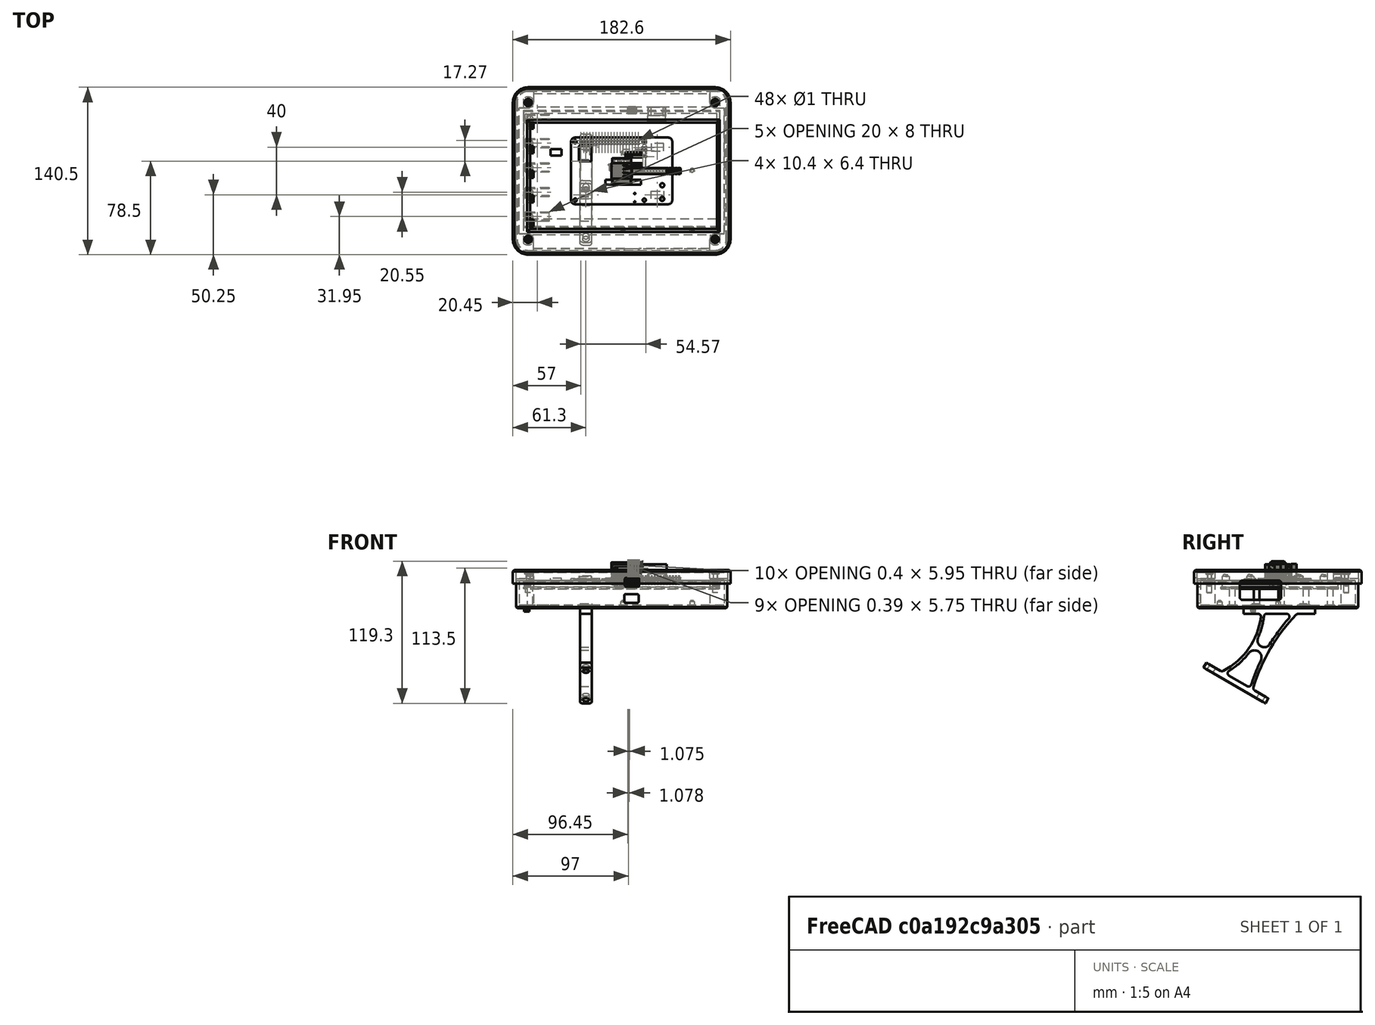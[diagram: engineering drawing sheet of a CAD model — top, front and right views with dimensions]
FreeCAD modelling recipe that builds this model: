
FCSTD DOCUMENT  (FreeCAD 0.19R24212 (Git))
Label: rpi_screen
License: Creative Commons Attribution
LicenseURL: http://creativecommons.org/licenses/by/4.0/
objects: Part::Feature×166, Part::Compound2×67, App::Part×24, App::Link×22, Sketcher::SketchObject×20, PartDesign::SubShapeBinder×13, PartDesign::Pocket×12, App::FeaturePython×10, PartDesign::Pad×9, Part::FeaturePython×8, PartDesign::Plane×5, PartDesign::Mirrored×4, PartDesign::Body×4, TechDraw::DrawViewDimension×4, PartDesign::Chamfer×3, PartDesign::LinearPattern×3, PartDesign::Fillet×3, Mesh::Feature×3, App::DocumentObjectGroup×2, PartDesign::MultiTransform×2, +9 more types
note: 286 computed .brp shape members not serialized (recipe doc carries the construction recipe); baked Part::Feature solids carry a one-line shape summary decoded from their .brp

FEATURE [Part::Feature] Compound  label="3"
  shape: bbox 164.9 x 124.4 x 20.55 mm, 570 faces, 2 solids (baked)
FEATURE [Part::Feature] Solid  label="pcb"
  shape: bbox 85 x 56 x 1.6 mm, 74 faces (baked)
FEATURE [Part::Feature] Solid001  label="shield"
  shape: bbox 5.846 x 7.775 x 3.404 mm, 350 faces (baked)
FEATURE [Part::Feature] Solid002  label="socket_housing"
  shape: bbox 4.232 x 6.852 x 2.152 mm, 218 faces (baked)
FEATURE [Part::Feature] Solid003  label="socket_plate"
  shape: bbox 3.38 x 6.8 x 0.31 mm, 84 faces (baked)
FEATURE [Part::Feature] Solid004  label="terminal"
  shape: bbox 3.22 x 0.35 x 1.72 mm, 36 faces (baked)
FEATURE [Part::Compound2] Compound001  label="shield:1"
  Links = -> [Solid001]
FEATURE [Part::Compound2] Compound002  label="socket_housing:1"
  Links = -> [Solid002]
FEATURE [Part::Compound2] Compound003  label="socket_plate:1"
  Links = -> [Solid003]
FEATURE [App::Link] Link  label="terminal:1"
  ElementCount = 5
  LinkedObject = -> Solid004
  PlacementList = 5 placements: [(0,0,0),(-4.44089e-15,-1.3,0),(-4.44089e-15,-0.65,0),(-4.44089e-15,0.65,0),(-4.44089e-15,1.3,0)]
  ScaleList = (5) [(1,1,1),(1,1,1),(1,1,1),(1,1,1),(1,1,1)]
  ShowElement = false
FEATURE [App::Part] Part  label="micro_usb_connector v17"
  Group = -> [Compound001,Compound002,Compound003,Link,Solid001,Solid002,Solid003]
  Origin = -> Origin
FEATURE [Part::Feature] Solid005  label="shell"
  shape: bbox 12 x 1.42 x 11.4 mm, 293 faces (baked)
FEATURE [Part::Compound2] Compound004  label="housing"
  Links = -> [Solid005]
FEATURE [Part::Feature] Solid006  label="base"
  shape: bbox 11.86 x 1.428 x 10.41 mm, 183 faces (baked)
FEATURE [Part::Feature] Solid007  label="Component12"
  shape: bbox 0.75 x 1.138 x 7.857 mm, 54 faces (baked)
FEATURE [Part::Feature] Solid008  label="Component13"
  shape: bbox 0.75 x 1.164 x 8.156 mm, 54 faces (baked)
FEATURE [Part::Feature] Solid009  label="Component14"
  shape: bbox 0.75 x 1.133 x 7.808 mm, 54 faces (baked)
FEATURE [Part::Feature] Solid010  label="Component15"
  shape: bbox 1.567 x 1.275 x 4.5 mm, 37 faces (baked)
FEATURE [Part::Feature] Solid011  label="Component16"
  shape: bbox 1.37 x 1.25 x 4.893 mm, 26 faces (baked)
FEATURE [App::Link] Link001  label="Component12:1"
  ElementCount = 5
  LinkedObject = -> Solid007
  PlacementList = 5 placements: [(0,0,0),(-2.2,0,-4.44089e-15),(-4.4,0,-4.44089e-15),(-6.6,0,-4.44089e-15),(-7.7,0,-4.44089e-15)]
  ScaleList = (5) [(1,1,1),(1,1,1),(1,1,1),(1,1,1),(1,1,1)]
  ShowElement = false
FEATURE [Part::Compound2] Compound005  label="Component13:1"
  Links = -> [Solid008]
  Placement = pos=(-1.1,6.29e-14,5.33e-14) rot=(0,0,1;0rad)
FEATURE [App::Link] Link002  label="Component14:1"
  ElementCount = 2
  LinkedObject = -> Solid009
  PlacementList = 2 placements: [(-3.3,3.34455e-14,5.32907e-14),(-5.5,2.90046e-14,5.32907e-14)]
  ScaleList = (2) [(1,1,1),(1,1,1)]
  ShowElement = false
FEATURE [Part::Compound2] Compound006  label="Component15:1"
  Links = -> [Solid010]
FEATURE [Part::Compound2] Compound007  label="Component16:1"
  Links = -> [Solid011]
FEATURE [App::Part] Part001  label="leads"
  Group = -> [Link001,Compound005,Link002,Compound006,Compound007,Solid008,Solid010,Solid011]
  Origin = -> Origin001
FEATURE [Part::Compound2] Compound008  label="housing:1"
  Links = -> [Compound004]
FEATURE [Part::Compound2] Compound009  label="base:1"
  Links = -> [Solid006]
FEATURE [Part::Compound2] Compound010  label="leads:1"
  Links = -> [Part001]
FEATURE [App::Part] Part002  label="sd_card_slot_molex v11"
  Group = -> [Compound008,Compound009,Compound010,Compound004,Solid005,Solid006,Part001]
  Origin = -> Origin002
FEATURE [Part::Feature] Compound011  label="pins"
  shape: bbox 48.9 x 3.175 x 10 mm, 560 faces, 40 solids (baked)
FEATURE [Part::Feature] Solid012  label="Component67"
  shape: bbox 50.81 x 5.089 x 2.549 mm, 625 faces (baked)
FEATURE [Part::Compound2] Compound012  label="spacers"
  Links = -> [Solid012]
FEATURE [Part::Compound2] Compound013  label="pins:1"
  Links = -> [Compound011]
FEATURE [Part::Compound2] Compound014  label="spacers:1"
  Links = -> [Compound012]
FEATURE [App::Part] Part003  label="Pin Header 20x2 TH Pitch 2.54mm v1"
  Group = -> [Compound013,Compound014,Compound011,Compound012,Solid012]
  Origin = -> Origin003
FEATURE [Part::Feature] Solid013  label="outer"
  shape: bbox 17 x 15.83 x 20.03 mm, 628 faces (baked)
FEATURE [Part::Feature] Solid014  label="back_shell"
  shape: bbox 2.8 x 13.7 x 13.5 mm, 64 faces (baked)
FEATURE [Part::Feature] Solid015  label="mid_cover"
  shape: bbox 8.5 x 12.4 x 5.09 mm, 174 faces (baked)
FEATURE [Part::Compound2] Compound015  label="outer:1"
  Links = -> [Solid013]
FEATURE [Part::Compound2] Compound016  label="back_shell:1"
  Links = -> [Solid014]
FEATURE [Part::Compound2] Compound017  label="mid_cover:1"
  Links = -> [Solid015]
FEATURE [App::Part] Part004  label="shell"
  Group = -> [Compound015,Compound016,Compound017,Solid013,Solid014,Solid015]
  Origin = -> Origin004
FEATURE [Part::Feature] Solid016  label="Component5"
  shape: bbox 16.28 x 12.43 x 15.05 mm, 451 faces (baked)
FEATURE [Part::Compound2] Compound018  label="Component4"
  Links = -> [Solid016]
FEATURE [Part::Feature] Solid017  label="top_lead"
  shape: bbox 14.29 x 1.538 x 16.6 mm, 94 faces (baked)
FEATURE [Part::Feature] Solid018  label="bottom_lead"
  shape: bbox 11.67 x 1.538 x 7.97 mm, 92 faces (baked)
FEATURE [App::Link] Link003  label="top_lead:1"
  ElementCount = 4
  LinkedObject = -> Solid017
  PlacementList = 4 placements: [(0,0,0),(0,-2.5,0),(0,-7,0),(0,-4.5,0)]
  ScaleList = (4) [(1,1,1),(1,1,1),(1,1,1),(1,1,1)]
  ShowElement = false
FEATURE [App::Link] Link004  label="bottom_lead:1"
  ElementCount = 4
  LinkedObject = -> Solid018
  PlacementList = 4 placements: [(0,0,0),(0,-7,0),(0,-2.5,0),(0,-4.5,0)]
  ScaleList = (4) [(1,1,1),(1,1,1),(1,1,1),(1,1,1)]
  ShowElement = false
FEATURE [App::Part] Part005  label="leads"
  Group = -> [Link003,Link004]
  Origin = -> Origin005
FEATURE [Part::Compound2] Compound019  label="shell:1"
  Links = -> [Part004]
FEATURE [Part::Compound2] Compound020  label="Component4:1"
  Links = -> [Compound018]
FEATURE [Part::Compound2] Compound021  label="leads:1"
  Links = -> [Part005]
FEATURE [App::Part] Part006  label="USB-A-stack-1x2 v23"
  Group = -> [Compound019,Compound020,Compound021,Part004,Compound018,Solid016,Part005]
  Origin = -> Origin006
FEATURE [App::Link] Link005  label="outer:1"
  LinkedObject = -> Solid013
FEATURE [App::Link] Link006  label="back_shell:1"
  LinkedObject = -> Solid014
FEATURE [App::Link] Link007  label="mid_cover:1"
  LinkedObject = -> Solid015
FEATURE [App::Part] Part007  label="shell"
  Group = -> [Link005,Link006,Link007]
  Origin = -> Origin007
FEATURE [App::Link] Link008  label="Component4"
  LinkedObject = -> Solid016
FEATURE [App::Link] Link009  label="top_lead:1"
  ElementCount = 4
  LinkedObject = -> Solid017
  PlacementList = 4 placements: [(0,0,0),(0,-2.5,0),(0,-7,0),(0,-4.5,0)]
  ScaleList = (4) [(1,1,1),(1,1,1),(1,1,1),(1,1,1)]
  ShowElement = false
FEATURE [App::Link] Link010  label="bottom_lead:1"
  ElementCount = 4
  LinkedObject = -> Solid018
  PlacementList = 4 placements: [(0,0,0),(0,-7,0),(0,-2.5,0),(0,-4.5,0)]
  ScaleList = (4) [(1,1,1),(1,1,1),(1,1,1),(1,1,1)]
  ShowElement = false
FEATURE [App::Part] Part008  label="leads"
  Group = -> [Link009,Link010]
  Origin = -> Origin008
FEATURE [Part::Compound2] Compound022  label="shell:1"
  Links = -> [Part007]
FEATURE [Part::Compound2] Compound023  label="Component4:1"
  Links = -> [Link008]
FEATURE [Part::Compound2] Compound024  label="leads:1"
  Links = -> [Part008]
FEATURE [App::Part] Part009  label="USB-A-stack-1x2 v23"
  Group = -> [Compound022,Compound023,Compound024,Part007,Link008,Part008]
  Origin = -> Origin009
FEATURE [Part::Feature] Compound025  label="te_1-1734248-5"
  shape: bbox 22.4 x 5.68 x 5.072 mm, 978 faces, 17 solids (baked)
FEATURE [Part::Feature] Compound026  label="pins"
  shape: bbox 3.175 x 3.175 x 10 mm, 56 faces, 4 solids (baked)
FEATURE [Part::Feature] Solid019  label="Component5"
  shape: bbox 5.089 x 5.089 x 2.549 mm, 67 faces (baked)
FEATURE [Part::Compound2] Compound027  label="spacers"
  Links = -> [Solid019]
FEATURE [Part::Compound2] Compound028  label="pins:1"
  Links = -> [Compound026]
FEATURE [Part::Compound2] Compound029  label="spacers:1"
  Links = -> [Compound027]
FEATURE [App::Part] Part010  label="Pin Header 2x2 TH Pitch 2.54mm v1"
  Group = -> [Compound028,Compound029,Compound026,Compound027,Solid019]
  Origin = -> Origin010
FEATURE [Part::Feature] Compound030  label="SOP-3_1.6mm"
  shape: bbox 1.6 x 1.559 x 0.6498 mm, 68 faces, 4 solids (baked)
FEATURE [Part::Feature] Solid020  label="shell"
  shape: bbox 16.2 x 21.35 x 16.35 mm, 324 faces (baked)
FEATURE [Part::Feature] Compound031  label="rj45"
  shape: bbox 13.46 x 13.45 x 4.487 mm, 170 faces, 9 solids (baked)
FEATURE [Part::Feature] Compound032  label="magnetics"
  shape: bbox 11.5 x 6.5 x 11.5 mm, 40 faces, 2 solids (baked)
FEATURE [Part::Feature] Compound033  label="leads"
  shape: bbox 13.9 x 7.95 x 8.72 mm, 162 faces, 9 solids (baked)
FEATURE [Part::Compound2] Compound034  label="rj45:1"
  Links = -> [Compound031]
FEATURE [Part::Compound2] Compound035  label="magnetics:1"
  Links = -> [Compound032]
FEATURE [Part::Compound2] Compound036  label="leads:1"
  Links = -> [Compound033]
FEATURE [App::Part] Part011  label="wiring"
  Group = -> [Compound034,Compound035,Compound036,Compound031,Compound032,Compound033]
  Origin = -> Origin011
FEATURE [Part::Feature] Solid021  label="base"
  shape: bbox 15.6 x 20.75 x 16.5 mm, 165 faces (baked)
FEATURE [Part::Feature] Compound037  label="led_org"
  shape: bbox 3.048 x 5.198 x 4.864 mm, 48 faces, 2 solids (baked)
FEATURE [Part::Feature] Compound038
  shape: bbox 13.8 x 4.169 x 2.2 mm, 12 faces, 2 solids (baked)
FEATURE [App::Link] Link011  label="led_org:1"
  ElementCount = 2
  LinkedObject = -> Compound037
  PlacementList = 2 placements: [(-5.37,0,2.2),(5.37,-8.88178e-15,2.2)]
  ScaleList = (2) [(1,1,1),(1,1,1)]
  ShowElement = false
FEATURE [App::Part] Part012  label="lights"
  Group = -> [Link011,Compound038]
  Origin = -> Origin012
FEATURE [Part::Compound2] Compound039  label="shell:1"
  Links = -> [Solid020]
FEATURE [Part::Compound2] Compound040  label="wiring:1"
  Links = -> [Part011]
FEATURE [Part::Compound2] Compound041  label="base:1"
  Links = -> [Solid021]
FEATURE [Part::Compound2] Compound042  label="lights:1"
  Links = -> [Part012]
FEATURE [App::Part] Part013  label="EDAC_1743_RJ45_TH v18"
  Group = -> [Compound039,Compound040,Compound041,Compound042,Solid020,Part011,Solid021,Part012]
  Origin = -> Origin013
FEATURE [Part::Feature] Compound043  label="qfn32_5mm v3"
  shape: bbox 5.2 x 5.2 x 0.55 mm, 218 faces, 33 solids (baked)
FEATURE [Part::Feature] Compound044  label="qfn48_9mm v3"
  shape: bbox 9 x 9 x 0.6 mm, 314 faces, 49 solids (baked)
FEATURE [Part::Feature] Compound045  label="TSOP-6 2mm v1"
  shape: bbox 2 x 2.009 x 0.7998 mm, 110 faces, 7 solids (baked)
FEATURE [Part::Feature] Compound046  label="TSOP-6 3mm v3"
  shape: bbox 3 x 2.913 x 0.7997 mm, 110 faces, 7 solids (baked)
FEATURE [Part::Feature] Solid022  label="Component1"
  shape: bbox 2.5 x 1.75 x 0.4 mm, 6 faces (baked)
FEATURE [Part::Feature] Compound047  label="lead"
  shape: bbox 2.7 x 1.95 x 0.12 mm, 96 faces, 16 solids (baked)
FEATURE [Part::Compound2] Compound048  label="Component1:1"
  Links = -> [Solid022]
  Placement = pos=(0,-1.3e-15,0) rot=(0,0,1;0rad)
FEATURE [Part::Compound2] Compound049  label="lead:1"
  Links = -> [Compound047]
  Placement = pos=(0,-1.3e-15,0) rot=(0,0,1;0rad)
FEATURE [App::Part] Part014  label="qfp16_3x2mm v5"
  Group = -> [Compound048,Compound049,Solid022,Compound047]
  Origin = -> Origin014
FEATURE [Part::Feature] Solid023  label="Component73"
  shape: bbox 10.5 x 13 x 2 mm, 46 faces (baked)
FEATURE [Part::Compound2] Compound050  label="wifi"
  Links = -> [Solid023]
FEATURE [Part::Feature] Compound051  label="qfn80_12mm v3"
  shape: bbox 12 x 12 x 0.6 mm, 506 faces, 81 solids (baked)
FEATURE [Part::Feature] Compound052  label="Component2"
  shape: bbox 3.2 x 2.5 x 0.3 mm, 44 faces, 4 solids (baked)
FEATURE [Part::Feature] Solid024  label="Component3"
  shape: bbox 3.2 x 2.5 x 0.4 mm, 30 faces (baked)
FEATURE [Part::Feature] Solid025  label="Component4"
  shape: bbox 2.9 x 2.3 x 0.2 mm, 35 faces (baked)
FEATURE [Part::Feature] Solid026  label="Component5"
  shape: bbox 2.5 x 1.9 x 0.2 mm, 35 faces (baked)
FEATURE [Part::Compound2] Compound053  label="Component2:1"
  Links = -> [Compound052]
FEATURE [Part::Compound2] Compound054  label="Component3:1"
  Links = -> [Solid024]
FEATURE [Part::Compound2] Compound055  label="Component4:1"
  Links = -> [Solid025]
FEATURE [Part::Compound2] Compound056  label="Component5:1"
  Links = -> [Solid026]
FEATURE [App::Part] Part015  label="crystal_dfn4 v1"
  Group = -> [Compound053,Compound054,Compound055,Compound056,Compound052,Solid024,Solid025,Solid026]
  Origin = -> Origin015
FEATURE [Part::Feature] Compound057  label="bcm2837 v8"
  shape: bbox 14 x 14 x 1.6 mm, 565 faces, 83 solids (baked)
FEATURE [Part::Feature] Compound058  label="wlbga140_5mm v2"
  shape: bbox 4.47 x 5.27 x 0.51 mm, 446 faces, 141 solids (baked)
FEATURE [Part::Feature] Compound059  label="cap0603_03 v2"
  shape: bbox 2.303 x 0.9021 x 0.802 mm, 98 faces, 3 solids (baked)
FEATURE [Part::Feature] Compound060  label="cap0402 v1"
  shape: bbox 1.367 x 0.6001 x 0.5 mm, 98 faces, 3 solids (baked)
FEATURE [Part::Feature] Compound061  label="resistor_0402 v1"
  shape: bbox 1.268 x 0.6007 x 0.3506 mm, 56 faces, 3 solids (baked)
FEATURE [Part::Feature] Compound062  label="cap1206 v4"
  shape: bbox 4.144 x 2.009 x 1.609 mm, 98 faces, 3 solids (baked)
FEATURE [Part::Feature] Compound063  label="ind2520 v1"
  shape: bbox 2.606 x 2.106 x 1.53 mm, 54 faces, 3 solids (baked)
FEATURE [Part::Feature] Compound064  label="ledra_0603 v2"
  shape: bbox 1.2 x 1.7 x 0.6 mm, 51 faces, 5 solids (baked)
FEATURE [Part::Feature] Solid027  label="tip_lead"
  shape: bbox 9.124 x 7.155 x 8.351 mm, 90 faces (baked)
FEATURE [Part::Feature] Solid028  label="Component2"
  shape: bbox 13.26 x 2.5 x 4.339 mm, 52 faces (baked)
FEATURE [Part::Feature] Solid029  label="Component3"
  shape: bbox 11.45 x 1.401 x 8.705 mm, 48 faces (baked)
FEATURE [Part::Feature] Solid030  label="Component4"
  shape: bbox 8.225 x 1.505 x 8.701 mm, 48 faces (baked)
FEATURE [Part::Feature] Solid031
  shape: bbox 15.01 x 7.008 x 7.255 mm, 115 faces (baked)
FEATURE [Part::Compound2] Compound065  label="tip_lead:1"
  Links = -> [Solid027]
FEATURE [Part::Compound2] Compound066  label="Component2:1"
  Links = -> [Solid028]
FEATURE [Part::Compound2] Compound067  label="Component3:1"
  Links = -> [Solid029]
FEATURE [Part::Compound2] Compound068  label="Component4:1"
  Links = -> [Solid030]
FEATURE [App::Part] Part016  label="pj-322 v8"
  Group = -> [Compound065,Compound066,Compound067,Compound068,Solid031,Solid027,Solid028,Solid029,Solid030]
  Origin = -> Origin016
FEATURE [Part::Feature] Compound069  label="SOP-3 v1"
  shape: bbox 3 x 2.713 x 1.05 mm, 68 faces, 4 solids (baked)
FEATURE [Part::Feature] Compound070  label="SOP-3 2.5mm v3"
  shape: bbox 2.6 x 2.213 x 0.6497 mm, 68 faces, 4 solids (baked)
FEATURE [Part::Feature] Compound071  label="capar2_1013 v1"
  shape: bbox 1.474 x 1.006 x 0.6909 mm, 170 faces, 5 solids (baked)
FEATURE [Part::Feature] Solid032  label="Component2"
  shape: bbox 15 x 11.55 x 8.274 mm, 347 faces (baked)
FEATURE [Part::Feature] Compound072
  shape: bbox 14.9 x 10.35 x 6.23 mm, 710 faces, 3 solids (baked)
FEATURE [Part::Compound2] Compound073  label="Component2:1"
  Links = -> [Solid032]
FEATURE [App::Part] Part017  label="molex hdmi smt v8"
  Group = -> [Compound073,Compound072,Solid032]
  Origin = -> Origin017
FEATURE [Part::Feature] Compound074  label="TSOP-2 4mm v2"
  shape: bbox 3.5 x 5.913 x 2.05 mm, 42 faces, 3 solids (baked)
FEATURE [Part::Compound2] Compound075  label="pcb:1"
  Links = -> [Solid]
FEATURE [Part::Compound2] Compound076  label="micro_usb_connector v17:1"
  Links = -> [Part]
  Placement = pos=(-31.9022,-25.6898,1.6) rot=(0,0,-1;1.5708rad)
FEATURE [Part::Compound2] Compound077  label="sd_card_slot_molex v11:1"
  Links = -> [Part002]
  Placement = pos=(-35.5259,0.0195459,0) rot=(0.57735,0.57735,-0.57735;4.18879rad)
FEATURE [Part::Compound2] Compound078  label="Pin Header 20x2 TH Pitch 2.54mm v1:1"
  Links = -> [Part003]
  Placement = pos=(-34.0983,24.2639,1.6) rot=(0,0,1;0rad)
FEATURE [Part::Compound2] Compound079  label="USB-A-stack-1x2 v23:1"
  Links = -> [Part006]
  Placement = pos=(35.9589,0.615691,1.6) rot=(0,0,1;0rad)
FEATURE [Part::Compound2] Compound080  label="USB-A-stack-1x2 v23:2"
  Links = -> [Part009]
  Placement = pos=(35.9589,19.0157,1.6) rot=(0,0,1;0rad)
FEATURE [App::Link] Link012  label="te_1-1734248-5:1"
  ElementCount = 2
  LinkedObject = -> Compound025
  PlacementList = 2 placements: [(-38.8804,0.0129527,1.58),(2.68293,-16.6511,1.58)]
  ScaleList = (2) [(1,1,1),(1,1,1)]
  ShowElement = false
FEATURE [Part::Compound2] Compound081  label="Pin Header 2x2 TH Pitch 2.54mm v1:1"
  Links = -> [Part010]
  Placement = pos=(17.7441,18.3632,1.6) rot=(0,0,1;0rad)
FEATURE [App::Link] Link013  label="SOP-3_1.6mm:1"
  ElementCount = 4
  LinkedObject = -> Compound030
  PlacementList = 4 placements: [(-40.8905,-10.8155,-8.403e-14),(-40.814,-18.4594,-8.42382e-14),(-16.6511,-13.2136,1.6),(-16.6511,-11.1136,1.6)]
  ScaleList = (4) [(1,1,1),(1,1,1),(1,1,1),(1,1,1)]
  ShowElement = false
FEATURE [Part::Compound2] Compound082  label="EDAC_1743_RJ45_TH v18:1"
  Links = -> [Part013]
  Placement = pos=(34.0212,-17.8853,1.5) rot=(0,0,1;1.5708rad)
FEATURE [Part::Compound2] Compound083  label="qfn32_5mm v3:1"
  Links = -> [Compound043]
  Placement = pos=(-29.2738,-12.9325,1.6) rot=(0,0,1;0rad)
FEATURE [Part::Compound2] Compound084  label="qfn48_9mm v3:1"
  Links = -> [Compound044]
  Placement = pos=(19.0565,-0.238451,1.6) rot=(0,0,1;0rad)
FEATURE [Part::Compound2] Compound085  label="TSOP-6 2mm v1:1"
  Links = -> [Compound045]
  Placement = pos=(14.2657,-10.6917,1.6) rot=(0,0,1;0rad)
FEATURE [Part::Compound2] Compound086  label="TSOP-6 3mm v3:1"
  Links = -> [Compound046]
  Placement = pos=(12.2743,17.7497,1.6) rot=(0,0,-1;1.5708rad)
FEATURE [Part::Compound2] Compound087  label="qfp16_3x2mm v5:1"
  Links = -> [Part014]
  Placement = pos=(-32.0595,4.91492,1.6) rot=(0,0,1;0rad)
FEATURE [Part::Compound2] Compound088  label="wifi:1"
  Links = -> [Compound050]
FEATURE [Part::Compound2] Compound089  label="qfn80_12mm v3:1"
  Links = -> [Compound051]
  Placement = pos=(0.978423,5.52192,4e-16) rot=(0,1,0;3.14159rad)
FEATURE [App::Link] Link014  label="crystal_dfn4 v1:1"
  ElementCount = 2
  LinkedObject = -> Part015
  PlacementList = 2 placements: [(-16.2394,-5.98323,-1.98875e-15),(11.4677,1.47513,6.08602e-15)]
  ScaleList = (2) [(1,1,1),(1,1,1)]
  ShowElement = false
FEATURE [Part::Compound2] Compound090  label="bcm2837 v8:1"
  Links = -> [Compound057]
  Placement = pos=(-15.6667,3.46142,1.6) rot=(0,0,1;0rad)
FEATURE [Part::Compound2] Compound091  label="wlbga140_5mm v2:1"
  Links = -> [Compound058]
  Placement = pos=(-30.4818,13.9472,1.6) rot=(0,0,1;0rad)
FEATURE [App::Link] Link015  label="cap0603_03 v2:1"
  ElementCount = 15
  LinkedObject = -> Compound059
  PlacementList = 15 placements: [(6.20173,12.0599,1.6),(-22.2778,-12.3124,1.6),(-22.2778,-13.6124,1.6),(-36.2901,-12.0302,1.6),(-36.2901,-13.3302,1.6),(-22.6025,-16.7071,1.6),(-31.9549,-9.07389,1.6),(-36.0614,-9.11907,1.6),(-16.8344,0.818806,-0.000650846),(-16.6946,6.87647,-0.000650846),(-40.1331,-7.59203,-0.000650846),(13.801,-4.8435,-0.000650846),(22.8947,7.02239,-0.000650846),(21.8412,4.90662,-0.000650846),+1 more]
  ScaleList = (15) [(1,1,1),(1,1,1),(1,1,1),(1,1,1),(1,1,1),(1,1,1),(1,1,1),(1,1,1),(1,1,1),(1,1,1),(1,1,1),(1,1,1),(1,1,1),(1,1,1),(1,1,1)]
  ShowElement = false
FEATURE [App::Link] Link016  label="cap0402 v1:1"
  ElementCount = 90
  LinkedObject = -> Compound060
  PlacementList = 90 placements: [(-1.68462,0.200917,1.6),(-3.61651,0.117459,1.6),(5.92099,0.258461,1.6),(3.98909,0.175003,1.6),(-2.07285,4.84427,1.6),(-3.73362,5.74918,1.6),(-1.7854,5.75983,1.6),(1.09272,2.11766,1.6),(-0.660114,2.54963,1.6),(-0.904466,7.62354,1.6),(4.53291,2.97061,1.6),(6.38708,2.45158,1.6),(6.35031,5.20918,1.6),(4.97764,5.87101,1.6),(2.18297,-0.0835865,1.6),(2.55763,11.2194,1.6),(0.128581,11.1773,1.6),+73 more]
  ScaleList = (90) [(1,1,1),(1,1,1),(1,1,1),(1,1,1),(1,1,1),(1,1,1),(1,1,1),(1,1,1),(1,1,1),(1,1,1),(1,1,1),(1,1,1),(1,1,1),(1,1,1),(1,1,1),(1,1,1),(1,1,1),(1,1,1),+72 more]
  ShowElement = false
FEATURE [App::Link] Link017  label="resistor_0402 v1:1"
  ElementCount = 57
  LinkedObject = -> Compound061
  PlacementList = 57 placements: [(13.5093,-0.0741632,1.6),(13.5249,2.06113,1.6),(13.7425,5.61112,1.6),(20.9328,7.1813,1.6),(21.7458,7.19308,1.6),(12.3038,-10.6968,1.6),(12.2911,-11.6977,1.6),(16.2822,-10.7348,1.6),(16.2949,-11.7484,1.6),(12.2922,-13.2114,1.6),(12.2703,-14.0987,1.6),(6.27571,-16.9459,1.6),(17.4427,-5.70402,1.6),(18.7432,-5.71563,1.6),(20.5313,-5.75046,1.6),(21.9594,-5.73885,1.6),(24.5889,-0.571464,1.6),+40 more]
  ScaleList = (57) [(1,1,1),(1,1,1),(1,1,1),(1,1,1),(1,1,1),(1,1,1),(1,1,1),(1,1,1),(1,1,1),(1,1,1),(1,1,1),(1,1,1),(1,1,1),(1,1,1),(1,1,1),(1,1,1),(1,1,1),(1,1,1),+39 more]
  ShowElement = false
FEATURE [App::Link] Link018  label="cap1206 v4:1"
  ElementCount = 11
  LinkedObject = -> Compound062
  PlacementList = 11 placements: [(7.98424,7.88741,1.6),(-25.9964,-19.3212,1.6),(-36.5363,-17.3583,1.6),(-22.3159,-8.61657,1.6),(-20.0447,-8.61657,1.6),(-26.8904,-24.2006,1.6),(23.3268,10.3578,1.6),(23.886,19.0543,1.6),(25.6036,-6.14103,1.6),(16.4512,-16.6927,1.6),(17.7022,-20.3318,1.6)]
  ScaleList = (11) [(1,1,1),(1,1,1),(1,1,1),(1,1,1),(1,1,1),(1,1,1),(1,1,1),(1,1,1),(1,1,1),(1,1,1),(1,1,1)]
  ShowElement = false
FEATURE [App::Link] Link019  label="ind2520 v1:1"
  ElementCount = 4
  LinkedObject = -> Compound063
  PlacementList = 4 placements: [(-33.8028,-16.3221,1.6),(-33.9058,-9.58662,1.6),(-24.8087,-16.2044,1.6),(-24.7831,-9.50136,1.6)]
  ScaleList = (4) [(1,1,1),(1,1,1),(1,1,1),(1,1,1)]
  ShowElement = false
FEATURE [App::Link] Link020  label="ledra_0603 v2:1"
  ElementCount = 2
  LinkedObject = -> Compound064
  PlacementList = 2 placements: [(-41.4207,-16.546,1.6),(-41.4207,-20.2157,1.6)]
  ScaleList = (2) [(1,1,1),(1,1,1)]
  ShowElement = false
FEATURE [Part::Compound2] Compound092  label="pj-322 v8:1"
  Links = -> [Part016]
  Placement = pos=(11.1035,-22.958,1.6) rot=(0,0,1;1.5708rad)
FEATURE [Part::Compound2] Compound093  label="SOP-3 v1:1"
  Links = -> [Compound069]
  Placement = pos=(-17.0907,-15.6679,1.6) rot=(0,0,1;1.5708rad)
FEATURE [Part::Compound2] Compound094  label="SOP-3 2.5mm v3:1"
  Links = -> [Compound070]
  Placement = pos=(7.13922,-13.3247,1.6) rot=(0,0,1;0rad)
FEATURE [App::Link] Link021  label="capar2_1013 v1:1"
  ElementCount = 4
  LinkedObject = -> Compound071
  PlacementList = 4 placements: [(-11.0324,-15.0395,1.6),(-9.5324,-15.0395,1.6),(-8.0324,-15.0395,1.6),(-6.5324,-15.0395,1.6)]
  ScaleList = (4) [(1,1,1),(1,1,1),(1,1,1),(1,1,1)]
  ShowElement = false
FEATURE [Part::Compound2] Compound095  label="molex hdmi smt v8:1"
  Links = -> [Part017]
  Placement = pos=(-10.5578,-23.8041,1.6) rot=(0,0,1;0rad)
FEATURE [Part::Compound2] Compound096  label="TSOP-2 4mm v2:1"
  Links = -> [Compound074]
  Placement = pos=(-23.9074,-24.0113,1.6) rot=(0,0,1;0rad)
FEATURE [App::Part] Part018  label="raspberry_pi_3_b_plus v38"
  Group = -> [Compound075,Compound076,Compound077,Compound078,Compound079,Compound080,Link012,Compound081,Link013,Compound082,Compound083,Compound084,Compound085,Compound086,Compound087,Compound088,Compound089,Link014,Compound090,Compound091,Link015,Link016,Link017,Link018,Link019,Link020,Compound092,Compound093,Compound094,Link021,Compound095,Compound096,Solid,Part,Part002,Part003,Part006,Part009,Part010,+16 more]
  Origin = -> Origin018
  Placement = pos=(40.15,24.4,17.75) rot=(1,0,0;3.14159rad)
FEATURE [Part::Feature] Solid033  label="1"
  shape: bbox 2.5 x 5 x 0.9 mm, 6 faces (baked)
FEATURE [Part::Feature] Solid034  label="2"
  shape: bbox 2.5 x 5 x 0.9 mm, 6 faces (baked)
FEATURE [Part::Feature] Solid035  label="3"
  shape: bbox 2.5 x 5 x 0.9 mm, 6 faces (baked)
FEATURE [Part::Feature] Solid036  label="4"
  shape: bbox 2.5 x 5 x 0.9 mm, 6 faces (baked)
FEATURE [Part::Feature] Solid037  label="6"
  shape: bbox 0.4 x 0.2 x 6.5 mm, 6 faces (baked)
FEATURE [Part::Feature] Solid038  label="7"
  shape: bbox 0.4 x 0.2 x 6.5 mm, 6 faces (baked)
FEATURE [Part::Feature] Solid039  label="8"
  shape: bbox 0.4 x 0.2 x 6.5 mm, 6 faces (baked)
FEATURE [Part::Feature] Solid040  label="9"
  shape: bbox 0.4 x 0.2 x 6.5 mm, 6 faces (baked)
FEATURE [Part::Feature] Solid041  label="10"
  shape: bbox 0.4 x 0.2 x 6.5 mm, 6 faces (baked)
FEATURE [Part::Feature] Solid042  label="11"
  shape: bbox 0.4 x 0.2 x 6.5 mm, 6 faces (baked)
FEATURE [Part::Feature] Solid043  label="12"
  shape: bbox 0.4 x 0.2 x 6.5 mm, 6 faces (baked)
FEATURE [Part::Feature] Solid044  label="13"
  shape: bbox 0.4 x 0.2 x 6.5 mm, 6 faces (baked)
FEATURE [Part::Feature] Solid045  label="14"
  shape: bbox 0.4 x 0.2 x 6.5 mm, 6 faces (baked)
FEATURE [Part::Feature] Solid046  label="15"
  shape: bbox 0.4 x 0.2 x 6.5 mm, 6 faces (baked)
FEATURE [Part::Feature] Solid047  label="16"
  shape: bbox 0.4 x 0.2 x 6.5 mm, 6 faces (baked)
FEATURE [Part::Feature] Solid048  label="17"
  shape: bbox 0.4 x 0.2 x 6.5 mm, 6 faces (baked)
FEATURE [Part::Feature] Solid049  label="18"
  shape: bbox 0.4 x 0.2 x 6.5 mm, 6 faces (baked)
FEATURE [Part::Feature] Solid050  label="19"
  shape: bbox 0.4 x 0.2 x 6.5 mm, 6 faces (baked)
FEATURE [Part::Feature] Solid051  label="20"
  shape: bbox 0.4 x 0.2 x 6.5 mm, 6 faces (baked)
FEATURE [Part::Feature] Solid052  label="21"
  shape: bbox 0.4 x 0.2 x 6.5 mm, 6 faces (baked)
FEATURE [Part::Feature] Solid053  label="22"
  shape: bbox 0.4 x 0.2 x 6.5 mm, 6 faces (baked)
FEATURE [Part::Feature] Solid054  label="23"
  shape: bbox 0.4 x 0.2 x 6.5 mm, 6 faces (baked)
FEATURE [Part::Feature] Solid055  label="24"
  shape: bbox 0.4 x 0.2 x 6.5 mm, 6 faces (baked)
FEATURE [Part::Feature] Solid056  label="25"
  shape: bbox 0.4 x 0.2 x 6.5 mm, 6 faces (baked)
FEATURE [Part::Feature] Solid057  label="26"
  shape: bbox 0.4 x 0.2 x 6.5 mm, 6 faces (baked)
FEATURE [Part::Feature] Solid058  label="27"
  shape: bbox 0.4 x 0.4828 x 5.951 mm, 23 faces (baked)
FEATURE [Part::Feature] Solid059  label="28"
  shape: bbox 0.4 x 0.4828 x 5.951 mm, 23 faces (baked)
FEATURE [Part::Feature] Solid060  label="29"
  shape: bbox 0.4 x 0.5578 x 6.051 mm, 25 faces (baked)
FEATURE [Part::Feature] Solid061  label="32"
  shape: bbox 0.4 x 0.5578 x 6.051 mm, 25 faces (baked)
FEATURE [Part::Feature] Solid062  label="33"
  shape: bbox 0.4 x 0.5578 x 6.051 mm, 25 faces (baked)
FEATURE [Part::Feature] Solid063  label="34"
  shape: bbox 0.4 x 0.5578 x 6.051 mm, 25 faces (baked)
FEATURE [Part::Feature] Solid064  label="35"
  shape: bbox 0.4 x 0.5578 x 6.051 mm, 25 faces (baked)
FEATURE [Part::Feature] Solid065  label="36"
  shape: bbox 0.4 x 0.5578 x 6.051 mm, 25 faces (baked)
FEATURE [Part::Feature] Solid066  label="37"
  shape: bbox 0.4 x 0.5578 x 6.051 mm, 25 faces (baked)
FEATURE [Part::Feature] Solid067  label="38"
  shape: bbox 0.4 x 0.5578 x 6.051 mm, 25 faces (baked)
FEATURE [Part::Feature] Solid068  label="39"
  shape: bbox 0.4 x 0.5578 x 6.051 mm, 25 faces (baked)
FEATURE [Part::Feature] Solid069  label="95"
  shape: bbox 1 x 1 x 1 mm, 6 faces (baked)
FEATURE [Part::Feature] Solid070  label="96"
  shape: bbox 1 x 1 x 1 mm, 6 faces (baked)
FEATURE [Part::Feature] Solid071  label="97"
  shape: bbox 1 x 1 x 1 mm, 6 faces (baked)
FEATURE [Part::Feature] Solid072  label="98"
  shape: bbox 1 x 1 x 1 mm, 6 faces (baked)
FEATURE [Part::Feature] Solid073  label="103"
  shape: bbox 20 x 18 x 0.9 mm, 26 faces (baked)
FEATURE [Part::Feature] Solid074  label="32"
  shape: bbox 0.4 x 0.5578 x 6.051 mm, 25 faces (baked)
FEATURE [Part::Feature] Solid075  label="27"
  shape: bbox 0.4 x 0.4828 x 5.951 mm, 23 faces (baked)
FEATURE [Part::Feature] Solid076  label="1"
  shape: bbox 13.3 x 3.9 x 6.525 mm, 432 faces (baked)
FEATURE [Part::Feature] Solid077  label="27"
  shape: bbox 0.4 x 0.4828 x 5.951 mm, 23 faces (baked)
FEATURE [Part::Feature] Solid078  label="27"
  shape: bbox 0.4 x 0.4828 x 5.951 mm, 23 faces (baked)
FEATURE [Part::Feature] Solid079  label="27"
  shape: bbox 0.4 x 0.4828 x 5.951 mm, 23 faces (baked)
FEATURE [Part::Feature] Solid080  label="27"
  shape: bbox 0.4 x 0.4828 x 5.951 mm, 23 faces (baked)
FEATURE [Part::Feature] Solid081  label="27"
  shape: bbox 0.4 x 0.4828 x 5.951 mm, 23 faces (baked)
FEATURE [Part::Feature] Solid082  label="27"
  shape: bbox 0.4 x 0.4828 x 5.951 mm, 23 faces (baked)
FEATURE [Part::Feature] Solid083  label="27"
  shape: bbox 0.4 x 0.4828 x 5.951 mm, 23 faces (baked)
FEATURE [Part::Feature] Solid084  label="5"
  shape: bbox 13.3 x 3.9 x 4.6 mm, 24 faces (baked)
FEATURE [Part::Feature] Solid085  label="1"
  shape: bbox 13.7 x 4.3 x 13.2 mm, 87 faces (baked)
FEATURE [Part::Feature] Solid086  label="39"
  shape: bbox 0.4 x 0.5578 x 6.051 mm, 25 faces (baked)
FEATURE [Part::Feature] Solid087  label="38"
  shape: bbox 0.4 x 0.5578 x 6.051 mm, 25 faces (baked)
FEATURE [Part::Feature] Solid088  label="37"
  shape: bbox 0.4 x 0.5578 x 6.051 mm, 25 faces (baked)
FEATURE [Part::Feature] Solid089  label="36"
  shape: bbox 0.4 x 0.5578 x 6.051 mm, 25 faces (baked)
FEATURE [Part::Feature] Solid090  label="35"
  shape: bbox 0.4 x 0.5578 x 6.051 mm, 25 faces (baked)
FEATURE [Part::Feature] Solid091  label="34"
  shape: bbox 0.4 x 0.5578 x 6.051 mm, 25 faces (baked)
FEATURE [Part::Feature] Solid092  label="33"
  shape: bbox 0.4 x 0.5578 x 6.051 mm, 25 faces (baked)
FEATURE [Part::Feature] Solid093  label="32"
  shape: bbox 0.4 x 0.5578 x 6.051 mm, 25 faces (baked)
FEATURE [Part::Feature] Solid094  label="29"
  shape: bbox 0.4 x 0.5578 x 6.051 mm, 25 faces (baked)
FEATURE [Part::Feature] Solid095  label="28"
  shape: bbox 0.4 x 0.4828 x 5.951 mm, 23 faces (baked)
FEATURE [Part::Feature] Solid096  label="27"
  shape: bbox 0.4 x 0.4828 x 5.951 mm, 23 faces (baked)
FEATURE [Part::Feature] Solid097  label="26"
  shape: bbox 0.4 x 0.2 x 6.5 mm, 6 faces (baked)
FEATURE [Part::Feature] Solid098  label="25"
  shape: bbox 0.4 x 0.2 x 6.5 mm, 6 faces (baked)
FEATURE [Part::Feature] Solid099  label="24"
  shape: bbox 0.4 x 0.2 x 6.5 mm, 6 faces (baked)
FEATURE [Part::Feature] Solid100  label="23"
  shape: bbox 0.4 x 0.2 x 6.5 mm, 6 faces (baked)
FEATURE [Part::Feature] Solid101  label="22"
  shape: bbox 0.4 x 0.2 x 6.5 mm, 6 faces (baked)
FEATURE [Part::Feature] Solid102  label="21"
  shape: bbox 0.4 x 0.2 x 6.5 mm, 6 faces (baked)
FEATURE [Part::Feature] Solid103  label="20"
  shape: bbox 0.4 x 0.2 x 6.5 mm, 6 faces (baked)
FEATURE [Part::Feature] Solid104  label="19"
  shape: bbox 0.4 x 0.2 x 6.5 mm, 6 faces (baked)
FEATURE [Part::Feature] Solid105  label="18"
  shape: bbox 0.4 x 0.2 x 6.5 mm, 6 faces (baked)
FEATURE [Part::Feature] Solid106  label="17"
  shape: bbox 0.4 x 0.2 x 6.5 mm, 6 faces (baked)
FEATURE [Part::Feature] Solid107  label="16"
  shape: bbox 0.4 x 0.2 x 6.5 mm, 6 faces (baked)
FEATURE [Part::Feature] Solid108  label="15"
  shape: bbox 0.4 x 0.2 x 6.5 mm, 6 faces (baked)
FEATURE [Part::Feature] Solid109  label="14"
  shape: bbox 0.4 x 0.2 x 6.5 mm, 6 faces (baked)
FEATURE [Part::Feature] Solid110  label="13"
  shape: bbox 0.4 x 0.2 x 6.5 mm, 6 faces (baked)
FEATURE [Part::Feature] Solid111  label="12"
  shape: bbox 0.4 x 0.2 x 6.5 mm, 6 faces (baked)
FEATURE [Part::Feature] Solid112  label="11"
  shape: bbox 0.4 x 0.2 x 6.5 mm, 6 faces (baked)
FEATURE [Part::Feature] Solid113  label="10"
  shape: bbox 0.4 x 0.2 x 6.5 mm, 6 faces (baked)
FEATURE [Part::Feature] Solid114  label="9"
  shape: bbox 0.4 x 0.2 x 6.5 mm, 6 faces (baked)
FEATURE [Part::Feature] Solid115  label="8"
  shape: bbox 0.4 x 0.2 x 6.5 mm, 6 faces (baked)
FEATURE [Part::Feature] Solid116  label="7"
  shape: bbox 0.4 x 0.2 x 6.5 mm, 6 faces (baked)
FEATURE [Part::Feature] Solid117  label="6"
  shape: bbox 0.4 x 0.2 x 6.5 mm, 6 faces (baked)
FEATURE [Part::Feature] Solid118  label="27"
  shape: bbox 0.4 x 0.4828 x 5.951 mm, 23 faces (baked)
FEATURE [Part::Feature] Solid119  label="27"
  shape: bbox 0.4 x 0.4828 x 5.951 mm, 23 faces (baked)
FEATURE [Part::Feature] Solid120  label="27"
  shape: bbox 0.4 x 0.4828 x 5.951 mm, 23 faces (baked)
FEATURE [Part::Feature] Solid121  label="27"
  shape: bbox 0.4 x 0.4828 x 5.951 mm, 23 faces (baked)
FEATURE [Part::Feature] Solid122  label="27"
  shape: bbox 0.4 x 0.4828 x 5.951 mm, 23 faces (baked)
FEATURE [Part::Feature] Solid123  label="27"
  shape: bbox 0.4 x 0.4828 x 5.951 mm, 23 faces (baked)
FEATURE [Part::Feature] Solid124  label="27"
  shape: bbox 0.4 x 0.4828 x 5.951 mm, 23 faces (baked)
FEATURE [Part::Feature] Solid125  label="1"
  shape: bbox 13.3 x 3.9 x 6.525 mm, 432 faces (baked)
FEATURE [Part::Feature] Solid126  label="27"
  shape: bbox 0.4 x 0.4828 x 5.951 mm, 23 faces (baked)
FEATURE [Part::Feature] Solid127  label="32"
  shape: bbox 0.4 x 0.5578 x 6.051 mm, 25 faces (baked)
FEATURE [Part::Feature] Solid128  label="98"
  shape: bbox 1 x 1 x 1 mm, 6 faces (baked)
FEATURE [Part::Feature] Solid129  label="97"
  shape: bbox 1 x 1 x 1 mm, 6 faces (baked)
FEATURE [Part::Feature] Solid130  label="96"
  shape: bbox 1 x 1 x 1 mm, 6 faces (baked)
FEATURE [Part::Feature] Solid131  label="95"
  shape: bbox 1 x 1 x 1 mm, 6 faces (baked)
FEATURE [Part::Feature] Solid132  label="2"
  shape: bbox 13.7 x 4.3 x 13.2 mm, 87 faces (baked)
FEATURE [Part::Feature] Solid133  label="5"
  shape: bbox 13.3 x 3.9 x 4.6 mm, 24 faces (baked)
FEATURE [Part::Feature] Solid134  label="3"
  shape: bbox 13.3 x 4.3 x 2 mm, 24 faces (baked)
FEATURE [Part::Feature] Solid135  label="4"
  shape: bbox 13.3 x 4.3 x 2 mm, 24 faces (baked)
FEATURE [App::Part] Part019  label="MCIB-HDMI~HDMI"
  Group = -> [Solid033,Solid034,Solid035,Solid036,Solid037,Solid038,Solid039,Solid040,Solid041,Solid042,Solid043,Solid044,Solid045,Solid046,Solid047,Solid048,Solid049,Solid050,Solid051,Solid052,Solid053,Solid054,Solid055,Solid056,Solid057,Solid058,Solid059,Solid060,Solid061,Solid062,Solid063,Solid064,Solid065,Solid066,Solid067,Solid068,Solid069,Solid070,Solid071,Solid072,Solid073,Solid074,Solid075,Solid076,+59 more]
  Origin = -> Origin019
  Placement = pos=(19.6,61.5,-1) rot=(1,0,0;1.5708rad)
FEATURE [Image::ImagePlane] ImagePlane
  Placement = pos=(1.6,4.1,-6.6) rot=(1,0,0;3.14159rad)
  XSize = 157
  YSize = 89
  expr: .Placement.Base.z = -6.8mm + 0.2mm
FEATURE [App::Part] Part020  label="Rpi+Screen"
  Group = -> [Compound,Part018,Part019,ImagePlane]
  Origin = -> Origin020
  Placement = pos=(0,0,0) rot=(1,0,0;3.14159rad)
FEATURE [App::FeaturePython] Dimension  # Draft dimension (typed FeaturePython)
  Diameter = false
  Dimline = (72.8752,-89.4803,-1.6)
  Direction = (0,0,0)
  Distance = 153.8
  End = (76.9,-57.45,1.6)
  Normal = (0,0,1)
  Start = (-76.9,-57.45,1.6)
FEATURE [App::FeaturePython] Dimension001  # Draft dimension (typed FeaturePython)
  Diameter = false
  Dimline = (-107.508,57.6749,-1.6)
  Direction = (0,0,0)
  Distance = 111.7
  End = (-78.5,55.85,1.6)
  Normal = (0,0,1)
  Start = (-78.5,-55.85,1.6)
FEATURE [App::FeaturePython] Dimension002  # Draft dimension (typed FeaturePython)
  Diameter = false
  Dimline = (78.2136,87.9866,-1.6)
  Direction = (0,0,0)
  Distance = 164.9
  End = (82.45,60.5994,1.6)
  Normal = (0,0,1)
  Start = (-82.45,60.5994,1.6)
FEATURE [App::FeaturePython] Dimension003  # Draft dimension (typed FeaturePython)
  Diameter = false
  Dimline = (-151.15,56.7407,-1.6)
  Direction = (0,0,0)
  Distance = 124.4
  End = (-78.5,62.2,1.6)
  Normal = (0,0,1)
  Start = (-78.5,-62.2,1.6)
FEATURE [App::FeaturePython] Dimension004  # Draft dimension (typed FeaturePython)
  Diameter = false
  Dimline = (82.45,75.3787,6.06086)
  Direction = (0,0,0)
  Distance = 6.9
  End = (82.45,60.5994,6.9)
  Normal = (1,0,0)
  Start = (82.45,60.5994,-7.4e-15)
FEATURE [App::FeaturePython] Dimension005  # Draft dimension (typed FeaturePython)
  Diameter = false
  Dimline = (82.45,-81.2954,-30.2204)
  Direction = (0,0,0)
  Distance = 19.35
  End = (79.55,-52.4,1.6)
  Normal = (1,0,0)
  Start = (79.55,-52.4,-17.75)
FEATURE [App::FeaturePython] Dimension006  # Draft dimension (typed FeaturePython)
  Diameter = false
  Dimline = (82.45,-147.448,5.12345)
  Direction = (0,0,0)
  Distance = 25.0389
  End = (82.45,-48.3947,6.9)
  Normal = (1,0,0)
  Start = (82.45,-48.3947,-18.1389)
FEATURE [PartDesign::SubShapeBinder] Binder
  BindMode = 0
  ClaimChildren = false
  Context = -> Part021 [Body.Binder.]
  Fuse = false
  MakeFace = true
  PartialLoad = false
  Relative = true
  Support = -> [Part020[Compound.Face122]]
  _Version = 2
FEATURE [Sketcher::SketchObject] Sketch
  ExternalGeometry = -> [Binder]
  FullyConstrained = true
  MapMode = 5
  Support = -> [XY_Plane]
  expr: Constraints[16] = <<Tableau>>.rayon_ext_boitier_inf
  sketch-geometry (8):
    g0: LineSegment StartX=-78.5 StartY=-67.45 StartZ=0 EndX=78.5 EndY=-67.45 EndZ=0
    g1: LineSegment StartX=88.5 StartY=-57.45 StartZ=0 EndX=88.5 EndY=57.45 EndZ=0
    g2: LineSegment StartX=78.5 StartY=67.45 StartZ=0 EndX=-78.5 EndY=67.45 EndZ=0
    g3: LineSegment StartX=-88.5 StartY=57.45 StartZ=0 EndX=-88.5 EndY=-57.45 EndZ=0
    g4: ArcOfCircle CenterX=78.5 CenterY=57.45 CenterZ=0 NormalX=0 NormalY=0 NormalZ=1 AngleXU=0 Radius=10 StartAngle=0 EndAngle=1.5708
    g5: ArcOfCircle CenterX=78.5 CenterY=-57.45 CenterZ=0 NormalX=0 NormalY=0 NormalZ=1 AngleXU=0 Radius=10 StartAngle=4.71239 EndAngle=6.28319
    g6: ArcOfCircle CenterX=-78.5 CenterY=-57.45 CenterZ=0 NormalX=0 NormalY=0 NormalZ=1 AngleXU=0 Radius=10 StartAngle=3.14159 EndAngle=4.71239
    g7: ArcOfCircle CenterX=-78.5 CenterY=57.45 CenterZ=0 NormalX=0 NormalY=0 NormalZ=1 AngleXU=0 Radius=10 StartAngle=1.5708 EndAngle=3.14159
  constraints (19):
    c: Horizontal(g0)
    c: Horizontal(g2)
    c: Vertical(g1)
    c: Vertical(g3)
    c: Tangent(g1,g4) = -1.5708
    c: Tangent(g2,g4) = -1.5708
    c: Tangent(g0,g5) = -1.5708
    c: Tangent(g1,g5) = -1.5708
    c: Tangent(g0,g6) = -1.5708
    c: Tangent(g3,g6) = -1.5708
    c: Tangent(g2,g7) = -1.5708
    c: Tangent(g3,g7) = -1.5708
    c: Equal(g7,g4)
    c: Coincident(g5,g-6)
    c: Coincident(g-3,g4)
    c: Coincident(g6,g-5)
    c: Radius(g4) = 10
    c: DistanceY(g0,g2) = 134.9
    c: DistanceX(g3,g1) = 177
FEATURE [PartDesign::Pad] Pad  label="Pad initial"
  Direction = (1,1,1)
  Length = 23
  Length2 = 100
  Profile = -> Sketch
  Refine = true
  Reversed = true
  Type = 0
FEATURE [Sketcher::SketchObject] Sketch001
  ExternalGeometry = -> [Binder,Sketch]
  FullyConstrained = true
  MapMode = 5
  Support = -> [XY_Plane]
  expr: Constraints[8] = <<Tableau>>.rayon
  expr: Constraints[1] = <<Tableau>>.B4
  sketch-geometry (20):
    g0: LineSegment StartX=-74 StartY=65.05 StartZ=0 EndX=74 EndY=65.05 EndZ=0
    g1: ArcOfCircle CenterX=78.5 CenterY=57.45 CenterZ=0 NormalX=0 NormalY=0 NormalZ=1 AngleXU=0 Radius=4.5 StartAngle=3.14159 EndAngle=4.71239
    g2: LineSegment StartX=86.1 StartY=52.95 StartZ=0 EndX=86.1 EndY=-52.95 EndZ=0
    g3: ArcOfCircle CenterX=78.5 CenterY=-57.45 CenterZ=0 NormalX=0 NormalY=0 NormalZ=1 AngleXU=0 Radius=4.5 StartAngle=1.5708 EndAngle=3.14159
    g4: LineSegment StartX=74 StartY=-65.05 StartZ=0 EndX=-74 EndY=-65.05 EndZ=0
    g5: ArcOfCircle CenterX=-78.5 CenterY=-57.45 CenterZ=0 NormalX=0 NormalY=0 NormalZ=1 AngleXU=0 Radius=4.5 StartAngle=6e-16 EndAngle=1.5708
    g6: LineSegment StartX=-86.1 StartY=-52.95 StartZ=0 EndX=-86.1 EndY=52.95 EndZ=0
    g7: ArcOfCircle CenterX=-78.5 CenterY=57.45 CenterZ=0 NormalX=0 NormalY=0 NormalZ=1 AngleXU=0 Radius=4.5 StartAngle=4.71239 EndAngle=6.28319
    g8: LineSegment StartX=74 StartY=65.05 StartZ=0 EndX=74 EndY=67.45 EndZ=0
    g9: LineSegment StartX=78.5 StartY=52.95 StartZ=0 EndX=86.1 EndY=52.95 EndZ=0
    g10: LineSegment StartX=74 StartY=57.45 StartZ=0 EndX=74 EndY=65.05 EndZ=0
    g11: LineSegment StartX=86.1 StartY=52.95 StartZ=0 EndX=88.5 EndY=52.95 EndZ=0
    g12: LineSegment StartX=86.1 StartY=-52.95 StartZ=0 EndX=78.5 EndY=-52.95 EndZ=0
    g13: LineSegment StartX=74 StartY=-65.05 StartZ=0 EndX=74 EndY=-57.45 EndZ=0
    g14: LineSegment StartX=74 StartY=-65.05 StartZ=0 EndX=74 EndY=-67.45 EndZ=0
    g15: LineSegment StartX=-74 StartY=-65.05 StartZ=0 EndX=-74 EndY=-57.45 EndZ=0
    g16: LineSegment StartX=-86.1 StartY=-52.95 StartZ=0 EndX=-78.5 EndY=-52.95 EndZ=0
    g17: LineSegment StartX=-86.1 StartY=52.95 StartZ=0 EndX=-78.5 EndY=52.95 EndZ=0
    g18: LineSegment StartX=-74 StartY=65.05 StartZ=0 EndX=-74 EndY=57.45 EndZ=0
    g19: LineSegment StartX=-88.5 StartY=52.95 StartZ=0 EndX=-86.1 EndY=52.95 EndZ=0
  constraints (52):
    c: Horizontal(g0)
    c: Distance(g0,g-7) = 2.4
    c: Coincident(g8,g0)
    c: PointOnObject(g8,g-7)
    c: Vertical(g8)
    c: Vertical(g6)
    c: Horizontal(g4)
    c: Vertical(g2)
    c: Radius(g1) = 4.5
    c: Equal(g7,g5)
    c: Equal(g5,g3)
    c: Equal(g3,g1)
    c: Coincident(g9,g2)
    c: Horizontal(g9)
    c: Coincident(g10,g0)
    c: Vertical(g10)
    c: Tangent(g1,g10) = 1.5708
    c: Tangent(g1,g9) = -1.5708
    c: Coincident(g1,g-6)
    c: Coincident(g11,g2)
    c: PointOnObject(g11,g-8)
    c: Horizontal(g11)
    c: Equal(g11,g8)
    c: Coincident(g12,g2)
    c: Horizontal(g12)
    c: Coincident(g13,g4)
    c: Vertical(g13)
    c: Tangent(g3,g13) = 1.5708
    c: Tangent(g3,g12) = -1.5708
    c: Coincident(g3,g-5)
    c: Coincident(g14,g4)
    c: PointOnObject(g14,g-10)
    c: Vertical(g14)
    c: Equal(g14,g11)
    c: Coincident(g15,g4)
    c: Vertical(g15)
    c: Coincident(g16,g6)
    c: Horizontal(g16)
    c: Tangent(g5,g16) = 1.5708
    c: Tangent(g5,g15) = -1.5708
    c: Coincident(g17,g6)
    c: Horizontal(g17)
    c: Tangent(g7,g17) = -1.5708
    c: Coincident(g18,g0)
    c: Vertical(g18)
    c: Tangent(g7,g18) = 1.5708
    c: Coincident(g19,g6)
    c: Horizontal(g19)
    c: PointOnObject(g19,g-9)
    c: Equal(g19,g8)
    c: Coincident(g7,g-3)
    c: Coincident(g5,g-4)
FEATURE [PartDesign::Pocket] Pocket  label="Evidement"
  BaseFeature = -> Pad
  Length = 0
  Length2 = 100
  Offset = -2.4
  Profile = -> Sketch001
  Refine = true
  Type = 3
  UpToFace = -> Pad [Face10]
  expr: Offset = -<<Tableau>>.B4
FEATURE [Spreadsheet::Sheet] Spreadsheet  label="Tableau"
  cells = A1=Data; A2=Diametre de buse; B2==0.4mm; B3=Épaisseur paroi; C3=Rayon; D3=rayon ext boitier inf; A4=Boitier bas; B4==6 * B2; C4(rayon)==4.5mm; D4(rayon_ext_boitier_inf)==10mm; A7=Boitier supérieur; C7(rayon_ext_boitier_sup)==D4 + B4 + B2
FEATURE [Sketcher::SketchObject] Sketch002
  ExternalGeometry = -> [Binder,Sketch001]
  FullyConstrained = false
  MapMode = 5
  Support = -> [XY_Plane]
  sketch-geometry (5):
    g0: Circle CenterX=78.5 CenterY=57.45 CenterZ=0 NormalX=0 NormalY=0 NormalZ=1 AngleXU=0 Radius=2.1
    g1: LineSegment StartX=76.6602 StartY=56.4374 StartZ=0 EndX=74.5577 EndY=55.2802 EndZ=0
    g2: Circle CenterX=78.5 CenterY=-57.45 CenterZ=0 NormalX=0 NormalY=0 NormalZ=1 AngleXU=0 Radius=2.1
    g3: Circle CenterX=-78.5 CenterY=-57.45 CenterZ=0 NormalX=0 NormalY=0 NormalZ=1 AngleXU=0 Radius=2.1
    g4: Circle CenterX=-78.5 CenterY=57.45 CenterZ=0 NormalX=0 NormalY=0 NormalZ=1 AngleXU=0 Radius=2.1
  constraints (13):
    c: Radius(g-3) = 1.6
    c: Coincident(g0,g-3)
    c: PointOnObject(g1,g0)
    c: PointOnObject(g1,g-7)
    c: Distance(g1) = 2.4
    c: PointOnObject(g0,g1)
    c: Coincident(g2,g-4)
    c: Coincident(g3,g-5)
    c: Coincident(g4,g-6)
    c: Equal(g4,g3)
    c: Equal(g3,g2)
    c: Equal(g2,g0)
    c: Radius(g0) = 2.1
FEATURE [PartDesign::Pocket] Pocket001  label="Insert"
  BaseFeature = -> Pocket
  Length = 10
  Length2 = 100
  Profile = -> Sketch002
  Refine = true
  Type = 0
FEATURE [PartDesign::SubShapeBinder] Binder001
  BindMode = 0
  ClaimChildren = false
  Context = -> Part021 [Body.Binder001.]
  Fuse = false
  MakeFace = true
  PartialLoad = false
  Relative = true
  Support = -> [Part020[Part018.Compound075.Face74]]
  _Version = 2
FEATURE [Sketcher::SketchObject] Sketch003
  AttachmentOffset = pos=(0,0,-20.6) rot=(0,0,1;0rad)
  ExternalGeometry = -> [Binder001]
  FullyConstrained = true
  MapMode = 5
  Placement = pos=(0,0,-20.6) rot=(0,0,1;0rad)
  Support = -> [XY_Plane]
  expr: .AttachmentOffset.Base.z = -Pad.Length + <<Tableau>>.B4
  sketch-geometry (4):
    g0: Circle CenterX=1.15 CenterY=-48.9 CenterZ=0 NormalX=0 NormalY=0 NormalZ=1 AngleXU=0 Radius=2
    g1: Circle CenterX=59.15 CenterY=-48.9 CenterZ=0 NormalX=0 NormalY=0 NormalZ=1 AngleXU=0 Radius=2
    g2: Circle CenterX=59.15 CenterY=0.1 CenterZ=0 NormalX=0 NormalY=0 NormalZ=1 AngleXU=0 Radius=2
    g3: Circle CenterX=1.15 CenterY=0.1 CenterZ=0 NormalX=0 NormalY=0 NormalZ=1 AngleXU=0 Radius=2
  constraints (8):
    c: Coincident(g0,g-4)
    c: Coincident(g1,g-5)
    c: Coincident(g2,g-6)
    c: Coincident(g3,g-3)
    c: Equal(g3,g2)
    c: Equal(g2,g1)
    c: Equal(g1,g0)
    c: Radius(g3) = 2
FEATURE [PartDesign::Pad] Pad001
  BaseFeature = -> Pocket001
  Direction = (1,1,1)
  Length = 10
  Length2 = 100
  Profile = -> Sketch003
  Refine = true
  Type = 3
  UpToFace = -> Binder001 [Face1]
FEATURE [Sketcher::SketchObject] Sketch004
  ExternalGeometry = -> [Binder001]
  FullyConstrained = true
  MapMode = 5
  Placement = pos=(0,-4.3e-15,-17.75) rot=(1,0,0;3.14159rad)
  Support = -> [Binder001]
  sketch-geometry (4):
    g0: Circle CenterX=1.15 CenterY=-0.1 CenterZ=0 NormalX=0 NormalY=0 NormalZ=1 AngleXU=0 Radius=1.2
    g1: Circle CenterX=59.15 CenterY=-0.1 CenterZ=0 NormalX=0 NormalY=0 NormalZ=1 AngleXU=0 Radius=1.2
    g2: Circle CenterX=59.15 CenterY=48.9 CenterZ=0 NormalX=0 NormalY=0 NormalZ=1 AngleXU=0 Radius=1.2
    g3: Circle CenterX=1.15 CenterY=48.9 CenterZ=0 NormalX=0 NormalY=0 NormalZ=1 AngleXU=0 Radius=1.2
  constraints (8):
    c: Coincident(g0,g-3)
    c: Coincident(g1,g-5)
    c: Coincident(g2,g-6)
    c: Coincident(g3,g-4)
    c: Equal(g3,g0)
    c: Equal(g0,g1)
    c: Equal(g1,g2)
    c: Radius(g0) = 1.2
FEATURE [PartDesign::Pad] Pad002
  BaseFeature = -> Pad001
  Direction = (1,1,1)
  Length = 1
  Length2 = 100
  Profile = -> Sketch004
  Refine = true
  Reversed = true
  Type = 0
FEATURE [PartDesign::Plane] DatumPlane
  AttachmentOffset = pos=(0,0,89) rot=(0,0,1;0rad)
  Length = 151.326
  MapMode = 5
  Placement = pos=(89,-1.98e-14,1.98e-14) rot=(0.57735,0.57735,0.57735;2.0944rad)
  ResizeMode = 0
  Support = -> [YZ_Plane]
  Width = 66.4256
FEATURE [PartDesign::SubShapeBinder] Binder002
  BindMode = 0
  ClaimChildren = false
  Context = -> Part022 [Body001.Binder002.]
  Fuse = false
  MakeFace = true
  PartialLoad = false
  Relative = true
  Support = -> [Part020[Compound.Face125]]
  _Version = 2
FEATURE [Sketcher::SketchObject] Sketch007
  ExternalGeometry = -> [Binder002]
  FullyConstrained = true
  MapMode = 5
  Support = -> [XY_Plane001]
  expr: Constraints[15] = <<Tableau>>.rayon_ext_boitier_sup
  sketch-geometry (8):
    g0: LineSegment StartX=-78.5 StartY=-70.25 StartZ=0 EndX=78.5 EndY=-70.25 EndZ=0
    g1: LineSegment StartX=91.3 StartY=-57.45 StartZ=0 EndX=91.3 EndY=57.45 EndZ=0
    g2: LineSegment StartX=78.5 StartY=70.25 StartZ=0 EndX=-78.5 EndY=70.25 EndZ=0
    g3: LineSegment StartX=-91.3 StartY=57.45 StartZ=0 EndX=-91.3 EndY=-57.45 EndZ=0
    g4: ArcOfCircle CenterX=78.5 CenterY=57.45 CenterZ=0 NormalX=0 NormalY=0 NormalZ=1 AngleXU=0 Radius=12.8 StartAngle=0 EndAngle=1.5708
    g5: ArcOfCircle CenterX=78.5 CenterY=-57.45 CenterZ=0 NormalX=0 NormalY=0 NormalZ=1 AngleXU=0 Radius=12.8 StartAngle=4.71239 EndAngle=6.28319
    g6: ArcOfCircle CenterX=-78.5 CenterY=-57.45 CenterZ=0 NormalX=0 NormalY=0 NormalZ=1 AngleXU=0 Radius=12.8 StartAngle=3.14159 EndAngle=4.71239
    g7: ArcOfCircle CenterX=-78.5 CenterY=57.45 CenterZ=0 NormalX=0 NormalY=0 NormalZ=1 AngleXU=0 Radius=12.8 StartAngle=1.5708 EndAngle=3.14159
  constraints (16):
    c: Horizontal(g0)
    c: Horizontal(g2)
    c: Vertical(g1)
    c: Tangent(g1,g4) = -1.5708
    c: Tangent(g2,g4) = -1.5708
    c: Tangent(g0,g5) = -1.5708
    c: Tangent(g1,g5) = -1.5708
    c: Tangent(g0,g6) = -1.5708
    c: Tangent(g3,g6) = -1.5708
    c: Tangent(g2,g7) = -1.5708
    c: Tangent(g3,g7) = -1.5708
    c: Coincident(g-6,g7)
    c: Coincident(g-5,g6)
    c: Coincident(g5,g-4)
    c: Coincident(g-3,g4)
    c: Radius(g4) = 12.8
FEATURE [PartDesign::Pad] Pad003  label="Pad init"
  Direction = (1,1,1)
  Length = 9
  Length2 = 100
  Profile = -> Sketch007
  Refine = true
  Type = 0
FEATURE [Sketcher::SketchObject] Sketch008
  ExternalGeometry = -> [Binder002]
  FullyConstrained = true
  MapMode = 5
  Placement = pos=(0,0,0) rot=(0,1,0;3.14159rad)
  Support = -> [XY_Plane001]
  expr: Constraints[15] = <<Tableau>>.C7 - <<Tableau>>.B4
  sketch-geometry (8):
    g0: LineSegment StartX=-78.5 StartY=-67.85 StartZ=0 EndX=78.5 EndY=-67.85 EndZ=0
    g1: LineSegment StartX=88.9 StartY=-57.45 StartZ=0 EndX=88.9 EndY=57.45 EndZ=0
    g2: LineSegment StartX=78.5 StartY=67.85 StartZ=0 EndX=-78.5 EndY=67.85 EndZ=0
    g3: LineSegment StartX=-88.9 StartY=57.45 StartZ=0 EndX=-88.9 EndY=-57.45 EndZ=0
    g4: ArcOfCircle CenterX=78.5 CenterY=57.45 CenterZ=0 NormalX=0 NormalY=0 NormalZ=1 AngleXU=0 Radius=10.4 StartAngle=0 EndAngle=1.5708
    g5: ArcOfCircle CenterX=78.5 CenterY=-57.45 CenterZ=0 NormalX=0 NormalY=0 NormalZ=1 AngleXU=0 Radius=10.4 StartAngle=4.71239 EndAngle=6.28319
    g6: ArcOfCircle CenterX=-78.5 CenterY=-57.45 CenterZ=0 NormalX=0 NormalY=0 NormalZ=1 AngleXU=0 Radius=10.4 StartAngle=3.14159 EndAngle=4.71239
    g7: ArcOfCircle CenterX=-78.5 CenterY=57.45 CenterZ=0 NormalX=0 NormalY=0 NormalZ=1 AngleXU=0 Radius=10.4 StartAngle=1.5708 EndAngle=3.14159
  constraints (16):
    c: Horizontal(g0)
    c: Horizontal(g2)
    c: Vertical(g1)
    c: Tangent(g1,g4) = -1.5708
    c: Tangent(g2,g4) = -1.5708
    c: Tangent(g0,g5) = -1.5708
    c: Tangent(g1,g5) = -1.5708
    c: Tangent(g0,g6) = -1.5708
    c: Tangent(g3,g6) = -1.5708
    c: Tangent(g2,g7) = -1.5708
    c: Tangent(g3,g7) = -1.5708
    c: Coincident(g-6,g7)
    c: Coincident(g-3,g4)
    c: Coincident(g-4,g5)
    c: Coincident(g6,g-5)
    c: Radius(g4) = 10.4
FEATURE [PartDesign::Pocket] Pocket004  label="Evidement"
  BaseFeature = -> Pad003
  Length = 7
  Length2 = 100
  Profile = -> Sketch008
  Refine = true
  Type = 0
FEATURE [PartDesign::SubShapeBinder] Binder003
  BindMode = 0
  ClaimChildren = false
  Context = -> Part022 [Body001.Binder003.]
  Fuse = false
  MakeFace = true
  PartialLoad = false
  Relative = true
  Support = -> [Part020[Compound.Face14]]
  _Version = 2
FEATURE [App::FeaturePython] Dimension007  # Draft dimension (typed FeaturePython)
  Diameter = false
  Dimline = (-69.8232,86.028,-6.9)
  Direction = (0,0,0)
  Distance = 5.5
  End = (-76.65,47.7,6.9)
  Normal = (0,0,1)
  Start = (-82.15,47.7,6.9)
FEATURE [App::FeaturePython] Dimension008  # Draft dimension (typed FeaturePython)
  Diameter = false
  Dimline = (-104.163,48.074,-6.9)
  Direction = (0,0,0)
  Distance = 7.3
  End = (-76.65,47.7,6.9)
  Normal = (0,0,1)
  Start = (-76.65,40.4,6.9)
FEATURE [App::FeaturePython] Dimension009  # Draft dimension (typed FeaturePython)
  Diameter = false
  Dimline = (85.1162,-72.8365,-6.9)
  Direction = (0,0,0)
  Distance = 2.5
  End = (82.15,-48.5,6.9)
  Normal = (0,0,1)
  Start = (79.65,-48.5,6.9)
FEATURE [App::DocumentObjectGroup] Groupe  label="Dimensions"
  Group = -> [Dimension,Dimension001,Dimension002,Dimension003,Dimension004,Dimension005,Dimension006,Dimension007,Dimension008,Dimension009]
FEATURE [Sketcher::SketchObject] Sketch009
  ExternalGeometry = -> [Binder003]
  FullyConstrained = true
  MapMode = 5
  Support = -> [XY_Plane001]
  sketch-geometry (8):
    g0: LineSegment StartX=-76.9 StartY=-48.75 StartZ=0 EndX=79.9 EndY=-48.75 EndZ=0
    g1: LineSegment StartX=79.9 StartY=-48.75 StartZ=0 EndX=79.9 EndY=40.65 EndZ=0
    g2: LineSegment StartX=79.9 StartY=40.65 StartZ=0 EndX=-76.9 EndY=40.65 EndZ=0
    g3: LineSegment StartX=-76.9 StartY=40.65 StartZ=0 EndX=-76.9 EndY=-48.75 EndZ=0
    g4: LineSegment StartX=79.65 StartY=40.4 StartZ=0 EndX=79.9 EndY=40.4 EndZ=0
    g5: LineSegment StartX=79.65 StartY=-48.5 StartZ=0 EndX=79.65 EndY=-48.75 EndZ=0
    g6: LineSegment StartX=-76.9 StartY=-48.5 StartZ=0 EndX=-76.65 EndY=-48.5 EndZ=0
    g7: LineSegment StartX=79.65 StartY=40.4 StartZ=0 EndX=79.65 EndY=40.65 EndZ=0
  constraints (24):
    c: Coincident(g0,g1)
    c: Coincident(g1,g2)
    c: Coincident(g2,g3)
    c: Coincident(g3,g0)
    c: Horizontal(g0)
    c: Horizontal(g2)
    c: Vertical(g1)
    c: Vertical(g3)
    c: Coincident(g4,g-6)
    c: PointOnObject(g4,g1)
    c: Horizontal(g4)
    c: Coincident(g5,g-6)
    c: PointOnObject(g5,g0)
    c: Vertical(g5)
    c: PointOnObject(g6,g3)
    c: Coincident(g6,g-5)
    c: Horizontal(g6)
    c: Coincident(g7,g4)
    c: PointOnObject(g7,g2)
    c: Vertical(g7)
    c: Equal(g4,g5)
    c: Equal(g5,g6)
    c: Equal(g6,g7)
    c: DistanceX(g4,g4) = 0.25
FEATURE [PartDesign::Pocket] Pocket005  label="ouverture écran"
  BaseFeature = -> Pocket004
  Length = 5
  Length2 = 100
  Profile = -> Sketch009
  Refine = true
  Reversed = true
  Type = 1
FEATURE [PartDesign::Plane] DatumPlane001
  AttachmentOffset = pos=(0,0,-7) rot=(0,0,1;0rad)
  Length = 214.635
  MapMode = 5
  Placement = pos=(0,0,7) rot=(0,1,0;3.14159rad)
  ResizeMode = 0
  Support = -> [XY_Plane001]
  Width = 172.535
  expr: .AttachmentOffset.Base.z = -Pocket004.Length
FEATURE [Sketcher::SketchObject] Sketch010
  ExternalGeometry = -> [Binder002]
  FullyConstrained = true
  MapMode = 5
  Placement = pos=(0,0,7) rot=(0,1,0;3.14159rad)
  Support = -> [DatumPlane001]
  expr: Constraints[13] = <<Tableau>>.rayon_ext_boitier_sup - <<Tableau>>.B2
  expr: Constraints[12] = <<Tableau>>.rayon
  sketch-geometry (6):
    g0: LineSegment StartX=74 StartY=-69.85 StartZ=0 EndX=74 EndY=-57.45 EndZ=0
    g1: ArcOfCircle CenterX=78.5 CenterY=-57.45 CenterZ=0 NormalX=0 NormalY=0 NormalZ=1 AngleXU=0 Radius=4.5 StartAngle=1.5708 EndAngle=3.14159
    g2: LineSegment StartX=78.5 StartY=-52.95 StartZ=0 EndX=90.9 EndY=-52.95 EndZ=0
    g3: LineSegment StartX=90.9 StartY=-52.95 StartZ=0 EndX=90.9 EndY=-57.45 EndZ=0
    g4: ArcOfCircle CenterX=78.5 CenterY=-57.45 CenterZ=0 NormalX=0 NormalY=0 NormalZ=1 AngleXU=0 Radius=12.4 StartAngle=4.71239 EndAngle=6.28319
    g5: LineSegment StartX=78.5 StartY=-69.85 StartZ=0 EndX=74 EndY=-69.85 EndZ=0
  constraints (14):
    c: Vertical(g0)
    c: Tangent(g0,g1) = 1.5708
    c: Tangent(g1,g2) = 1.5708
    c: Coincident(g2,g3)
    c: Vertical(g3)
    c: Tangent(g3,g4) = 1.5708
    c: Tangent(g4,g5) = 1.5708
    c: Coincident(g5,g0)
    c: Coincident(g1,g-3)
    c: Coincident(g4,g1)
    c: Horizontal(g5)
    c: Horizontal(g2)
    c: Radius(g1) = 4.5
    c: Radius(g4) = 12.4
FEATURE [PartDesign::Pad] Pad004  label="support ecran"
  BaseFeature = -> Pocket005
  Direction = (1,1,1)
  Length = 10
  Length2 = 100
  Profile = -> Sketch010
  Refine = true
  Reversed = true
  Type = 3
  UpToFace = -> Binder002 [Face1]
FEATURE [PartDesign::Mirrored] Mirrored
  MirrorPlane = -> YZ_Plane001
  Refine = true
FEATURE [PartDesign::Mirrored] Mirrored001
  MirrorPlane = -> XZ_Plane001
  Refine = true
FEATURE [PartDesign::MultiTransform] MultiTransform
  BaseFeature = -> Pad004
  Originals = -> [Pad004]
  Refine = true
  Transformations = -> [Mirrored,Mirrored001]
FEATURE [PartDesign::Plane] DatumPlane002
  AttachmentOffset = pos=(0,0,9) rot=(0,0,1;0rad)
  Length = 214.635
  MapMode = 5
  Placement = pos=(0,0,9) rot=(0,0,1;0rad)
  ResizeMode = 0
  Support = -> [XY_Plane001]
  Width = 172.535
  expr: .AttachmentOffset.Base.z = Pad003.Length
FEATURE [Sketcher::SketchObject] Sketch011
  ExternalGeometry = -> [Binder002]
  FullyConstrained = true
  MapMode = 5
  Placement = pos=(0,0,9) rot=(0,0,1;0rad)
  Support = -> [DatumPlane002]
  sketch-geometry (4):
    g0: Circle CenterX=78.5 CenterY=57.45 CenterZ=0 NormalX=0 NormalY=0 NormalZ=1 AngleXU=0 Radius=2.5
    g1: Circle CenterX=-78.5 CenterY=57.45 CenterZ=0 NormalX=0 NormalY=0 NormalZ=1 AngleXU=0 Radius=2.5
    g2: Circle CenterX=-78.5 CenterY=-57.45 CenterZ=0 NormalX=0 NormalY=0 NormalZ=1 AngleXU=0 Radius=2.5
    g3: Circle CenterX=78.5 CenterY=-57.45 CenterZ=0 NormalX=0 NormalY=0 NormalZ=1 AngleXU=0 Radius=2.5
  constraints (8):
    c: Coincident(g1,g-6)
    c: Coincident(g2,g-5)
    c: Coincident(g3,g-4)
    c: Equal(g3,g2)
    c: Equal(g2,g1)
    c: Equal(g1,g0)
    c: Coincident(g0,g-3)
    c: Radius(g0) = 2.5
FEATURE [PartDesign::Hole] Hole
  BaseFeature = -> MultiTransform
  Depth = 25
  DepthType = 0
  Diameter = 3.6
  DrillForDepth = false
  DrillPoint = 1
  DrillPointAngle = 118
  HoleCutCountersinkAngle = 90
  HoleCutCustomValues = false
  HoleCutDepth = 3.4
  HoleCutDiameter = 6.1
  HoleCutType = 1
  ModelActualThread = false
  Profile = -> Sketch011
  Refine = true
  Tapered = false
  TaperedAngle = 90
  ThreadAngle = 0
  ThreadClass = 0
  ThreadCutOffInner = 0
  ThreadCutOffOuter = 0
  ThreadDirection = 0
  ThreadFit = 2
  ThreadPitch = 0
  ThreadSize = 9
  ThreadType = 1
  Threaded = false
FEATURE [PartDesign::SubShapeBinder] Binder004
  BindMode = 0
  ClaimChildren = false
  Context = -> Part022 [Body001.Binder004.]
  Fuse = false
  MakeFace = true
  PartialLoad = false
  Relative = true
  Support = -> [Hole[Face4]]
  _Version = 2
FEATURE [PartDesign::Pad] Pad005
  BaseFeature = -> Hole
  Direction = (1,1,1)
  Length = 2.4
  Length2 = 100
  Profile = -> Binder004
  Refine = true
  Type = 0
  expr: Length = <<Tableau>>.B4
FEATURE [PartDesign::SubShapeBinder] Binder005
  BindMode = 0
  ClaimChildren = false
  Context = -> Part022 [Body001.Binder005.]
  Fuse = false
  MakeFace = true
  PartialLoad = false
  Relative = true
  Support = -> [Body[Pocket002.Sketch005.]]
  _Version = 2
FEATURE [PartDesign::Pocket] Pocket006
  BaseFeature = -> Pad005
  Length = 9.6
  Length2 = 100
  Midplane = true
  Profile = -> Binder005 [Face1]
  Refine = true
  Reversed = true
  Type = 0
  expr: Length = <<Tableau>>.B4 * 4
FEATURE [PartDesign::SubShapeBinder] Binder006
  BindMode = 0
  ClaimChildren = false
  Context = -> Part022 [Body001.Binder006.]
  Fuse = false
  MakeFace = true
  PartialLoad = false
  Relative = true
  Support = -> [Body[Pocket003.Sketch006.]]
  _Version = 2
FEATURE [PartDesign::Pocket] Pocket007
  BaseFeature = -> Pocket006
  Length = 9.6
  Length2 = 100
  Midplane = true
  Profile = -> Binder006
  Refine = true
  Type = 0
  expr: Length = <<Tableau>>.B4 * 4
FEATURE [PartDesign::SubShapeBinder] Binder007
  BindMode = 0
  ClaimChildren = false
  Context = -> Part022 [Body001.Binder007.]
  Fuse = false
  MakeFace = true
  PartialLoad = false
  Relative = true
  Support = -> [Part020[Compound.Face2]]
  _Version = 2
FEATURE [PartDesign::Chamfer] Chamfer001  label="Chanfrein écran"
  Angle = 45
  Base = -> Pocket007 [Edge89,Edge88,Edge91,Edge90]
  BaseFeature = -> Pocket007
  ChamferType = 1
  FlipDirection = false
  Refine = true
  Size = 2.4
  Size2 = 1.2
  SupportTransform = false
  expr: Size2 = <<Tableau>>.B4 / 2
  expr: Size = <<Tableau>>.B4
FEATURE [PartDesign::Chamfer] Chamfer002  label="Chanfrein périphérie"
  Angle = 45
  Base = -> Chamfer001 [Edge8]
  BaseFeature = -> Chamfer001
  ChamferType = 0
  FlipDirection = false
  Refine = true
  Size = 1.2
  Size2 = 1
  SupportTransform = false
  expr: Size = <<Tableau>>.B4 / 2
FEATURE [PartDesign::SubShapeBinder] Binder008
  BindMode = 0
  ClaimChildren = false
  Context = -> Part021 [Body.Binder008.]
  Fuse = false
  MakeFace = true
  PartialLoad = false
  Relative = true
  Support = -> [Part020[Compound.Edge128,Compound.Edge136]]
  _Version = 2
FEATURE [PartDesign::SubShapeBinder] Binder009
  BindMode = 0
  ClaimChildren = false
  Context = -> Part021 [Body.Binder009.]
  Fuse = false
  MakeFace = true
  PartialLoad = false
  Relative = true
  Support = -> [Part020[Compound.Edge365,Compound.Edge925]]
  _Version = 2
FEATURE [PartDesign::SubShapeBinder] Binder010
  BindMode = 0
  ClaimChildren = false
  Context = -> Part021 [Body.Binder010.]
  Fuse = false
  MakeFace = true
  PartialLoad = false
  Relative = true
  Support = -> [Part020[Part018.Compound076.Edge439]]
  _Version = 2
FEATURE [Sketcher::SketchObject] Sketch006
  AttachmentOffset = pos=(0,0,69) rot=(0,0,1;0rad)
  ExternalGeometry = -> [Binder008,Binder009,Binder010]
  FullyConstrained = true
  MapMode = 5
  Placement = pos=(0,-69,-1.53e-14) rot=(1,0,0;1.5708rad)
  Support = -> [XZ_Plane]
  expr: Constraints[15] = <<Tableau>>.B2 * 30
  sketch-geometry (13):
    g0: LineSegment StartX=3.87439 StartY=2.425 StartZ=0 EndX=13.4744 EndY=2.425 EndZ=0
    g1: LineSegment StartX=14.6744 StartY=1.225 StartZ=0 EndX=14.6744 EndY=-3.875 EndZ=0
    g2: LineSegment StartX=13.4744 StartY=-5.075 StartZ=0 EndX=3.87439 EndY=-5.075 EndZ=0
    g3: LineSegment StartX=2.67439 StartY=-3.875 StartZ=0 EndX=2.67439 EndY=1.225 EndZ=0
    g4: ArcOfCircle CenterX=3.87439 CenterY=1.225 CenterZ=0 NormalX=0 NormalY=0 NormalZ=1 AngleXU=0 Radius=1.2 StartAngle=1.5708 EndAngle=3.14159
    g5: ArcOfCircle CenterX=13.4744 CenterY=1.225 CenterZ=0 NormalX=0 NormalY=0 NormalZ=1 AngleXU=0 Radius=1.2 StartAngle=0 EndAngle=1.5708
    g6: ArcOfCircle CenterX=13.4744 CenterY=-3.875 CenterZ=0 NormalX=0 NormalY=0 NormalZ=1 AngleXU=0 Radius=1.2 StartAngle=4.71239 EndAngle=6.28319
    g7: ArcOfCircle CenterX=3.87439 CenterY=-3.875 CenterZ=0 NormalX=0 NormalY=0 NormalZ=1 AngleXU=0 Radius=1.2 StartAngle=3.14159 EndAngle=4.71239
    g8: GeomPoint X=8.67439 Y=-1.369 Z=0
    g9: LineSegment StartX=8.67439 StartY=-1.369 StartZ=0 EndX=8.67439 EndY=-1.624 EndZ=0
    g10: LineSegment StartX=11.0744 StartY=-0.15 StartZ=0 EndX=11.0744 EndY=2.425 EndZ=0
    g11: LineSegment StartX=11.7744 StartY=-2.5 StartZ=0 EndX=11.7744 EndY=-5.075 EndZ=0
    g12: LineSegment StartX=8.24488 StartY=-16.15 StartZ=0 EndX=8.67439 EndY=-2.5 EndZ=0
  constraints (33):
    c: Horizontal(g0)
    c: Horizontal(g2)
    c: Vertical(g1)
    c: Vertical(g3)
    c: Tangent(g0,g4) = 1.5708
    c: Tangent(g3,g4) = 1.5708
    c: Tangent(g0,g5) = 1.5708
    c: Tangent(g1,g5) = 1.5708
    c: Tangent(g1,g6) = 1.5708
    c: Tangent(g2,g6) = 1.5708
    c: Tangent(g2,g7) = 1.5708
    c: Tangent(g3,g7) = 1.5708
    c: Equal(g4,g5)
    c: Equal(g5,g6)
    c: Equal(g6,g7)
    c: DistanceX(g3,g1) = 12
    c: Radius(g5) = 1.2
    c: DistanceY(g2,g0) = 7.5
    c: Symmetric(g-3,g-4,g8)
    c: Coincident(g9,g8)
    c: Equal(g9,g-4)
    c: Symmetric(g3,g1,g9)
    c: Coincident(g10,g-6)
    c: PointOnObject(g10,g0)
    c: Vertical(g10)
    c: Coincident(g11,g-5)
    c: PointOnObject(g11,g2)
    c: Vertical(g11)
    c: Equal(g11,g10)
    c: DistanceY(g-7,g-5) = 13.65
    c: Distance(g12) = 13.6568
    c: Symmetric(g-5,g-5,g12)
    c: Coincident(g12,g-7)
FEATURE [PartDesign::SubShapeBinder] Binder011
  BindMode = 0
  ClaimChildren = false
  Context = -> Part021 [Body.Binder011.]
  Fuse = false
  MakeFace = true
  PartialLoad = false
  Relative = true
  Support = -> [Part020[Part018.Compound079.Edge1280,Part018.Compound080.Edge1280,Part018.Compound079.Edge1555,Part018.Compound080.Edge1286]]
  _Version = 2
FEATURE [Sketcher::SketchObject] Sketch005
  ExternalGeometry = -> [Binder011]
  FullyConstrained = true
  MapMode = 5
  Placement = pos=(89,-1.98e-14,1.98e-14) rot=(0.57735,0.57735,0.57735;2.0944rad)
  Support = -> [DatumPlane]
  sketch-geometry (14):
    g0: LineSegment StartX=-29.5843 StartY=-16.175 StartZ=0 EndX=0.415691 EndY=-16.175 EndZ=0
    g1: LineSegment StartX=2.81569 StartY=-13.775 StartZ=0 EndX=2.81569 EndY=-2.175 EndZ=0
    g2: LineSegment StartX=0.415691 StartY=0.225 StartZ=0 EndX=-29.5843 EndY=0.225 EndZ=0
    g3: LineSegment StartX=-31.9843 StartY=-2.175 StartZ=0 EndX=-31.9843 EndY=-13.775 EndZ=0
    g4: ArcOfCircle CenterX=-29.5843 CenterY=-2.175 CenterZ=0 NormalX=0 NormalY=0 NormalZ=1 AngleXU=0 Radius=2.4 StartAngle=1.5708 EndAngle=3.14159
    g5: ArcOfCircle CenterX=0.415691 CenterY=-2.175 CenterZ=0 NormalX=0 NormalY=0 NormalZ=1 AngleXU=0 Radius=2.4 StartAngle=0 EndAngle=1.5708
    g6: ArcOfCircle CenterX=0.415691 CenterY=-13.775 CenterZ=0 NormalX=0 NormalY=0 NormalZ=1 AngleXU=0 Radius=2.4 StartAngle=4.71239 EndAngle=6.28319
    g7: ArcOfCircle CenterX=-29.5843 CenterY=-13.775 CenterZ=0 NormalX=0 NormalY=0 NormalZ=1 AngleXU=0 Radius=2.4 StartAngle=3.14159 EndAngle=4.71239
    g8: GeomPoint X=-14.5843 Y=-7.975 Z=0
    g9: LineSegment StartX=-23.7843 StartY=-0.5 StartZ=0 EndX=-31.9843 EndY=-0.5 EndZ=0
    g10: LineSegment StartX=-29.5843 StartY=0.225 StartZ=0 EndX=-31.9843 EndY=0.225 EndZ=0
    g11: LineSegment StartX=-31.9843 StartY=0.225 StartZ=0 EndX=-31.9843 EndY=-2.175 EndZ=0
    g12: LineSegment StartX=0.415691 StartY=0.225 StartZ=0 EndX=2.81569 EndY=0.225 EndZ=0
    g13: LineSegment StartX=2.81569 StartY=0.225 StartZ=0 EndX=2.81569 EndY=-2.175 EndZ=0
  constraints (34):
    c: Horizontal(g0)
    c: Horizontal(g2)
    c: Vertical(g1)
    c: Vertical(g3)
    c: Tangent(g2,g4) = -1.5708
    c: Tangent(g3,g4) = -1.5708
    c: Tangent(g1,g5) = -1.5708
    c: Tangent(g2,g5) = -1.5708
    c: Tangent(g0,g6) = -1.5708
    c: Tangent(g1,g6) = -1.5708
    c: Tangent(g0,g7) = -1.5708
    c: Tangent(g3,g7) = -1.5708
    c: Equal(g4,g5)
    c: Equal(g5,g6)
    c: Equal(g6,g7)
    c: DistanceX(g3,g1) = 34.8
    c: DistanceY(g0,g2) = 16.4
    c: Symmetric(g-3,g-4,g8)
    c: Symmetric(g7,g5,g8)
    c: Horizontal(g9)
    c: DistanceX(g9,g9) = 8.2
    c: PointOnObject(g9,g3)
    c: Symmetric(g-5,g-5,g9)
    c: Radius(g5) = 2.4
    c: Horizontal(g10)
    c: Coincident(g10,g11)
    c: Vertical(g11)
    c: Horizontal(g12)
    c: Coincident(g12,g13)
    c: Vertical(g13)
    c: Coincident(g10,g2)
    c: Coincident(g11,g3)
    c: Coincident(g2,g12)
    c: Coincident(g1,g13)
FEATURE [PartDesign::Pocket] Pocket002  label="USB"
  BaseFeature = -> Pad002
  Length = 3
  Length2 = 100
  Profile = -> Sketch005
  Refine = true
  Type = 0
  UpToFace = -> Pad002 [Face21]
FEATURE [PartDesign::Pocket] Pocket003  label="µUSB"
  BaseFeature = -> Pocket002
  Length = 5
  Length2 = 100
  Profile = -> Sketch006
  Refine = true
  Type = 0
FEATURE [PartDesign::LinearPattern] LinearPattern  label="Repetition µUSB"
  BaseFeature = -> Pocket003
  Direction = -> Sketch006 [Axis3]
  Length = 13.66
  Occurrences = 2
  Originals = -> [Pocket003]
  Refine = true
  Reversed = true
FEATURE [PartDesign::Chamfer] Chamfer
  Angle = 45
  Base = -> LinearPattern [Face5]
  BaseFeature = -> LinearPattern
  ChamferType = 0
  FlipDirection = false
  Refine = true
  Size = 0.8
  Size2 = 1
  SupportTransform = false
FEATURE [PartDesign::Fillet] Fillet  label="Congé USB"
  Base = -> Chamfer002 [Edge111,Edge113]
  BaseFeature = -> Chamfer002
  Radius = 2.4
  Refine = true
  SupportTransform = false
  expr: Radius = <<Tableau>>.B4
FEATURE [PartDesign::Body] Body001  label="Boîtier supérieur"
  Group = -> [Binder002,Sketch007,Pad003,Sketch008,Pocket004,Binder003,Sketch009,Pocket005,DatumPlane001,Sketch010,Pad004,MultiTransform,Mirrored,Mirrored001,DatumPlane002,Sketch011,Hole,Binder004,Pad005,Binder005,Pocket006,Binder006,Pocket007,Binder007,Chamfer001,Chamfer002,Fillet]
  Origin = -> Origin022
  Tip = -> Fillet
FEATURE [Part::FeaturePython] Screw  label="M3x10-Screw"  # Fasteners workbench fastener (typed FeaturePython)
  Placement = pos=(78.5,-57.45,5.6) rot=(0,0,1;0rad)
  baseObject = -> Fillet [Edge182]
  diameter = 4
  invert = false
  length = 3
  lengthCustom = 10
  matchOuter = false
  offset = 0
  thread = false
  type = 32
FEATURE [Part::FeaturePython] Screw001  label="M3x10-Screw"  # Fasteners workbench fastener (typed FeaturePython)
  Placement = pos=(78.5,57.45,5.6) rot=(0,0,1;0rad)
  baseObject = -> Body001 [Edge162]
  diameter = 4
  invert = false
  length = 3
  lengthCustom = 10
  matchOuter = false
  offset = 0
  thread = false
  type = 32
FEATURE [Part::FeaturePython] Screw003  label="M3x10-Screw"  # Fasteners workbench fastener (typed FeaturePython)
  Placement = pos=(-78.5,-57.45,5.6) rot=(0,0,1;0rad)
  baseObject = -> Fillet [Edge190]
  diameter = 4
  invert = false
  length = 3
  lengthCustom = 10
  matchOuter = false
  offset = 0
  thread = false
  type = 32
FEATURE [Part::FeaturePython] Screw004  label="M3x10-Screw"  # Fasteners workbench fastener (typed FeaturePython)
  Placement = pos=(-78.5,57.45,5.6) rot=(0,0,1;0rad)
  baseObject = -> Body001 [Edge86]
  diameter = 4
  invert = false
  length = 3
  lengthCustom = 10
  matchOuter = false
  offset = 0
  thread = false
  type = 32
FEATURE [App::Part] Part022  label="Ensemble boîter sup"
  Group = -> [Screw001,Screw,Screw003,Body001,Screw004]
  Origin = -> Origin024
FEATURE [Mesh::Feature] Mesh004  label="Boîtier supérieur (Meshed)"
FEATURE [TechDraw::DrawSVGTemplate] Template
  EditableTexts = Designed_by_Name=Designed by Name; Drawing_number=Drawing number; FC-Date=Date; FC-SC=Scale; FC-SH=Sheet; FC-Title=Title; Subtitle=Subtitle; Weight=Weight
  Height = 210
  Orientation = 1
  Width = 297
FEATURE [TechDraw::DrawViewPart] View
  CoarseView = false
  Direction = (0,0,1)
  Focus = 100
  HardHidden = false
  IsoCount = 0
  IsoHidden = false
  IsoVisible = false
  LockPosition = false
  Perspective = false
  Rotation = 0
  ScaleType = 0
  SeamHidden = false
  SeamVisible = true
  SmoothHidden = false
  SmoothVisible = true
  Source = -> [Body001]
  X = 164.295
  XDirection = (1,0,0)
  Y = 121.676
FEATURE [TechDraw::DrawViewDimension] Dimension010
  Arbitrary = false
  ArbitraryTolerances = false
  EqualTolerance = true
  FormatSpec = ⌀%.0f
  FormatSpecOverTolerance = %+.0f
  FormatSpecUnderTolerance = %+.0f
  Inverted = false
  LockPosition = false
  MeasureType = 1
  OverTolerance = 0
  References2D = -> [View]
  Rotation = 0
  ScaleType = 0
  TheoreticalExact = false
  Type = 5
  UnderTolerance = 0
  X = 111.76
  Y = 57.4531
FEATURE [TechDraw::DrawViewDimension] Dimension011
  Arbitrary = false
  ArbitraryTolerances = false
  EqualTolerance = true
  FormatSpec = ⌀%.0f
  FormatSpecOverTolerance = %+.0f
  FormatSpecUnderTolerance = %+.0f
  Inverted = false
  LockPosition = false
  MeasureType = 1
  OverTolerance = 0
  References2D = -> [View]
  Rotation = 0
  ScaleType = 0
  TheoreticalExact = false
  Type = 5
  UnderTolerance = 0
  X = 104.223
  Y = 69.0506
FEATURE [TechDraw::DrawViewSection] SectionView  label="Section  - "
  BaseView = -> View
  CoarseView = false
  CutSurfaceDisplay = 2
  Direction = (1,0,0)
  FileGeomPattern = <path>
  FileHatchPattern = <path>
  Focus = 100
  FuseBeforeCut = false
  HardHidden = false
  HatchScale = 1
  IsoCount = 0
  IsoHidden = false
  IsoVisible = false
  LockPosition = false
  NameGeomPattern = Diamant
  Perspective = false
  Rotation = 0
  ScaleType = 0
  SeamHidden = false
  SeamVisible = true
  SectionDirection = 1
  SectionNormal = (1,0,0)
  SectionOrigin = (-79,0,3.3)
  SmoothHidden = false
  SmoothVisible = true
  Source = -> [Body001]
  X = 37.5703
  XDirection = (0,0,-1)
  Y = 122.09
FEATURE [TechDraw::DrawViewDimension] Dimension012
  Arbitrary = false
  ArbitraryTolerances = false
  EqualTolerance = true
  FormatSpec = %.0f
  FormatSpecOverTolerance = %+.0f
  FormatSpecUnderTolerance = %+.0f
  Inverted = false
  LockPosition = false
  MeasureType = 1
  OverTolerance = 0
  References2D = -> [SectionView]
  Rotation = 0
  ScaleType = 0
  TheoreticalExact = false
  Type = 1
  UnderTolerance = 0
  X = 7.89676
  Y = -47.5241
FEATURE [TechDraw::DrawViewDimension] Dimension013
  Arbitrary = false
  ArbitraryTolerances = false
  EqualTolerance = true
  FormatSpec = %.0f
  FormatSpecOverTolerance = %+.0f
  FormatSpecUnderTolerance = %+.0f
  Inverted = false
  LockPosition = false
  MeasureType = 1
  OverTolerance = 0
  References2D = -> [SectionView]
  Rotation = 0
  ScaleType = 0
  TheoreticalExact = false
  Type = 1
  UnderTolerance = 0
  X = 10.3861
  Y = -42.6061
FEATURE [TechDraw::DrawPage] Page
  KeepUpdated = false
  NextBalloonIndex = 1
  ProjectionType = 0
  Template = -> Template
  Views = -> [View,Dimension010,Dimension011,SectionView,Dimension012,Dimension013]
FEATURE [PartDesign::SubShapeBinder] Binder012
  BindMode = 0
  ClaimChildren = false
  Context = -> Part021 [Body.Binder012.]
  Fuse = false
  MakeFace = true
  PartialLoad = false
  Relative = true
  Support = -> [Part020[Compound.Face191,Compound.Face192,Compound.Face193,Compound.Face194,Compound.Face195]]
  _Version = 2
FEATURE [PartDesign::Plane] DatumPlane003
  AttachmentOffset = pos=(0,0,-20.6) rot=(0,0,1;0rad)
  Length = 207.905
  MapMode = 5
  Placement = pos=(0,0,-20.6) rot=(0,0,1;0rad)
  ResizeMode = 0
  Support = -> [XY_Plane]
  Width = 165.805
  expr: .AttachmentOffset.Base.z = -Pad.Length + Spreadsheet.B4
FEATURE [Sketcher::SketchObject] Sketch012
  ExternalGeometry = -> [Binder012]
  FullyConstrained = true
  MapMode = 5
  Placement = pos=(0,0,-20.6) rot=(0,0,1;0rad)
  Support = -> [DatumPlane003]
  sketch-geometry (1):
    g0: Circle CenterX=-76.85 CenterY=-38.3 CenterZ=0 NormalX=0 NormalY=0 NormalZ=1 AngleXU=0 Radius=2.4
  constraints (2):
    c: Coincident(g0,g-3)
    c: Radius(g0) = 2.4
FEATURE [PartDesign::Pad] Pad006
  BaseFeature = -> Chamfer
  Direction = (1,1,1)
  Length = 15
  Length2 = 100
  Offset = -0.4
  Profile = -> Sketch012
  Refine = true
  Type = 0
FEATURE [Sketcher::SketchObject] Sketch013
  ExternalGeometry = -> [Binder012]
  FullyConstrained = true
  MapMode = 5
  Placement = pos=(0,0,-20.6) rot=(0,0,1;0rad)
  Support = -> [DatumPlane003]
  sketch-geometry (11):
    g0: LineSegment StartX=-60.85 StartY=-35.5 StartZ=0 EndX=-79.65 EndY=-35.5 EndZ=0
    g1: LineSegment StartX=-79.65 StartY=-35.5 StartZ=0 EndX=-79.65 EndY=-41.1 EndZ=0
    g2: LineSegment StartX=-79.65 StartY=-41.1 StartZ=0 EndX=-60.85 EndY=-41.1 EndZ=0
    g3: LineSegment StartX=-60.85 StartY=-41.1 StartZ=0 EndX=-60.85 EndY=-42.3 EndZ=0
    g4: LineSegment StartX=-60.85 StartY=-42.3 StartZ=0 EndX=-80.85 EndY=-42.3 EndZ=0
    g5: LineSegment StartX=-80.85 StartY=-42.3 StartZ=0 EndX=-80.85 EndY=-34.3 EndZ=0
    g6: LineSegment StartX=-80.85 StartY=-34.3 StartZ=0 EndX=-60.85 EndY=-34.3 EndZ=0
    g7: LineSegment StartX=-60.85 StartY=-34.3 StartZ=0 EndX=-60.85 EndY=-35.5 EndZ=0
    g8: LineSegment StartX=-80.85 StartY=-35.5 StartZ=0 EndX=-79.65 EndY=-35.5 EndZ=0
    g9: LineSegment StartX=-79.65 StartY=-38.3 StartZ=0 EndX=-76.85 EndY=-38.3 EndZ=0
    g10: LineSegment StartX=-76.85 StartY=-38.3 StartZ=0 EndX=-76.85 EndY=-35.5 EndZ=0
  constraints (32):
    c: Horizontal(g0)
    c: Coincident(g0,g1)
    c: Vertical(g1)
    c: Coincident(g1,g2)
    c: Horizontal(g2)
    c: Coincident(g2,g3)
    c: Vertical(g3)
    c: Coincident(g3,g4)
    c: Horizontal(g4)
    c: Coincident(g4,g5)
    c: Vertical(g5)
    c: Coincident(g5,g6)
    c: Horizontal(g6)
    c: Coincident(g6,g7)
    c: Coincident(g7,g0)
    c: Vertical(g7)
    c: PointOnObject(g8,g5)
    c: Coincident(g8,g0)
    c: Horizontal(g8)
    c: Equal(g8,g7)
    c: Equal(g7,g3)
    c: Equal(g4,g6)
    c: Coincident(g9,g-3)
    c: Horizontal(g9)
    c: Coincident(g10,g9)
    c: PointOnObject(g10,g0)
    c: Vertical(g10)
    c: Equal(g10,g9)
    c: Symmetric(g1,g1,g9)
    c: DistanceY(g7,g7) = 1.2
    c: DistanceX(g9,g9) = 2.8
    c: DistanceX(g6,g6) = 20
FEATURE [PartDesign::Pocket] Pocket008
  BaseFeature = -> Pad006
  Length = 5
  Length2 = 100
  Profile = -> Sketch013
  Refine = true
  Type = 1
FEATURE [PartDesign::SubtractiveSphere] Sphere
  Angle1 = -90
  Angle2 = 90
  Angle3 = 360
  AttacherType = Attacher::AttachEngine3D
  AttachmentOffset = pos=(0,0,22) rot=(0,0,1;0rad)
  BaseFeature = -> Pocket008
  MapMode = 11
  Placement = pos=(-76.85,-38.3,-27.1) rot=(0.707107,-0.707107,0;3.14159rad)
  Radius = 4.8
  Refine = true
  Support = -> [Binder012]
FEATURE [PartDesign::Fillet] Fillet001
  Base = -> Sphere [Edge178,Edge174,Edge176,Edge180]
  BaseFeature = -> Sphere
  Placement = pos=(-76.85,-38.3,-27.1) rot=(0.707107,-0.707107,0;3.14159rad)
  Radius = 0.8
  Refine = true
  SupportTransform = false
FEATURE [PartDesign::LinearPattern] LinearPattern001
  BaseFeature = -> Fillet001
  Direction = -> Sketch012 [V_Axis]
  Length = 82.2
  Occurrences = 5
  Originals = -> [Pad006,Pocket008,Sphere,Fillet001]
  Placement = pos=(-76.85,-38.3,-27.1) rot=(0.707107,-0.707107,0;3.14159rad)
  Refine = true
FEATURE [Sketcher::SketchObject] Sketch014
  FullyConstrained = true
  MapMode = 5
  Placement = pos=(0,0,0) rot=(0.57735,0.57735,0.57735;2.0944rad)
  Support = -> [YZ_Plane004]
  sketch-geometry (13):
    g0: LineSegment StartX=-25.9808 StartY=60 StartZ=0 EndX=25.9808 EndY=90 EndZ=0
    g1: LineSegment StartX=-30 StartY=0 StartZ=0 EndX=-30 EndY=4.8 EndZ=0
    g2: LineSegment StartX=-30 StartY=4.8 StartZ=0 EndX=-15 EndY=4.8 EndZ=0
    g3: LineSegment StartX=30 StartY=4.8 StartZ=0 EndX=30 EndY=0 EndZ=0
    g4: LineSegment StartX=-30 StartY=0 StartZ=0 EndX=30 EndY=0 EndZ=0
    g5: LineSegment StartX=-25.9808 StartY=60 StartZ=0 EndX=-23.5808 EndY=55.8431 EndZ=0
    g6: LineSegment StartX=-23.5808 StartY=55.8431 StartZ=0 EndX=-10.5904 EndY=63.3431 EndZ=0
    g7: LineSegment StartX=25.9808 StartY=90 StartZ=0 EndX=28.3808 EndY=85.8431 EndZ=0
    g8: LineSegment StartX=28.3808 StartY=85.8431 StartZ=0 EndX=15.3904 EndY=78.3431 EndZ=0
    g9: ArcOfCircle CenterX=-64.9763 CenterY=38.002 CenterZ=0 NormalX=0 NormalY=0 NormalZ=1 AngleXU=0 Radius=60 StartAngle=5.69679 EndAngle=6.71922
    g10: ArcOfCircle CenterX=160.616 CenterY=40.7996 CenterZ=0 NormalX=0 NormalY=0 NormalZ=1 AngleXU=0 Radius=150 StartAngle=2.88861 EndAngle=3.38396
    g11: LineSegment StartX=15 StartY=4.8 StartZ=0 EndX=30 EndY=4.8 EndZ=0
    g12: GeomPoint X=0 Y=75 Z=0
  constraints (37):
    c: Vertical(g1)
    c: Coincident(g1,g2)
    c: Horizontal(g2)
    c: Coincident(g11,g3)
    c: Vertical(g3)
    c: Coincident(g1,g4)
    c: Horizontal(g4)
    c: Coincident(g0,g5)
    c: Coincident(g5,g6)
    c: Coincident(g0,g7)
    c: Coincident(g7,g8)
    c: Coincident(g9,g6)
    c: Coincident(g10,g8)
    c: Parallel(g6,g8)
    c: Parallel(g6,g0)
    c: Coincident(g2,g9)
    c: Coincident(g11,g10)
    c: Tangent(g2,g11)
    c: Perpendicular(g0,g5)
    c: Perpendicular(g7,g0)
    c: PointOnObject(g6,g8)
    c: Equal(g6,g8)
    c: Coincident(g4,g3)
    c: DistanceY(g1,g1) = 4.8  'epaisseur_base'
    c: DistanceX(g4,g4) = 60
    c: Equal(g2,g11)
    c: Equal(g1,g5)
    c: Distance(g0) = 60
    c: Angle(g0) = 0.523599
    c: Symmetric(g4,g4,g-1)
    c: Radius(g9) = 60
    c: Radius(g10) = 150
    c: DistanceX(g2,g2) = 15
    c: Symmetric(g0,g0,g12)
    c: PointOnObject(g12,g-2)
    c: Equal(g6,g2)
    c: DistanceY(g1,g0) = 60
FEATURE [PartDesign::Pad] Pad007
  Direction = (1,1,1)
  Length = 10
  Length2 = 100
  Midplane = true
  Placement = pos=(0,0,0) rot=(0.57735,0.57735,0.57735;2.0944rad)
  Profile = -> Sketch014
  Refine = true
  Type = 0
FEATURE [Sketcher::SketchObject] Sketch016
  ExternalGeometry = -> [Pad007]
  FullyConstrained = true
  MapMode = 5
  Placement = pos=(0,0,0) rot=(0.57735,0.57735,0.57735;2.0944rad)
  Support = -> [YZ_Plane004]
  sketch-geometry (8):
    g0: LineSegment StartX=-7.96507 StartY=4.8 StartZ=0 EndX=9.50645 EndY=4.8 EndZ=0
    g1: ArcOfCircle CenterX=9.50645 CenterY=7.2 CenterZ=0 NormalX=0 NormalY=0 NormalZ=1 AngleXU=0 Radius=2.4 StartAngle=4.71239 EndAngle=6.50198
    g2: ArcOfCircle CenterX=160.616 CenterY=40.7996 CenterZ=0 NormalX=0 NormalY=0 NormalZ=1 AngleXU=0 Radius=152.4 StartAngle=3.21745 EndAngle=3.36039
    g3: ArcOfCircle CenterX=2.73635 CenterY=28.8 CenterZ=0 NormalX=0 NormalY=0 NormalZ=1 AngleXU=0 Radius=5.93504 StartAngle=0.075859 EndAngle=3.00652
    g4: ArcOfCircle CenterX=-64.9763 CenterY=38.002 CenterZ=0 NormalX=0 NormalY=0 NormalZ=1 AngleXU=0 Radius=62.4 StartAngle=5.78784 EndAngle=6.14812
    g5: ArcOfCircle CenterX=-7.96507 CenterY=7.2 CenterZ=0 NormalX=0 NormalY=0 NormalZ=1 AngleXU=0 Radius=2.4 StartAngle=2.64624 EndAngle=4.71239
    g6: LineSegment StartX=-10.0766 StartY=8.34081 StartZ=0 EndX=-12.1881 EndY=9.48163 EndZ=0
    g7: LineSegment StartX=11.8492 StartY=7.72092 StartZ=0 EndX=14.192 EndY=8.24185 EndZ=0
  constraints (21):
    c: Horizontal(g0)
    c: Tangent(g0,g1) = -1.5708
    c: Tangent(g1,g2) = 1.5708
    c: Tangent(g2,g3) = 1.5708
    c: Tangent(g3,g4) = 1.5708
    c: Tangent(g4,g5) = 1.5708
    c: Tangent(g0,g5) = -1.5708
    c: PointOnObject(g-3,g0)
    c: Coincident(g4,g-3)
    c: Coincident(g2,g-4)
    c: Coincident(g6,g4)
    c: PointOnObject(g6,g-3)
    c: PointOnObject(g4,g6)
    c: Coincident(g7,g1)
    c: PointOnObject(g7,g-4)
    c: PointOnObject(g2,g7)
    c: Equal(g6,g7)
    c: Equal(g5,g1)
    c: Radius(g1) = 2.4
    c: Distance(g7) = 2.4
    c: Distance(g3,g0) = 24
FEATURE [Sketcher::SketchObject] Sketch015
  ExternalGeometry = -> [Sketch014,Sketch016]
  FullyConstrained = true
  MapMode = 5
  Placement = pos=(0,0,0) rot=(0.57735,0.57735,0.57735;2.0944rad)
  Support = -> [YZ_Plane004]
  sketch-geometry (9):
    g0: LineSegment StartX=-6.62652 StartY=65.6316 StartZ=0 EndX=7.76452 EndY=73.9403 EndZ=0
    g1: ArcOfCircle CenterX=8.96452 CenterY=71.8618 CenterZ=0 NormalX=0 NormalY=0 NormalZ=1 AngleXU=0 Radius=2.4 StartAngle=6.08115 EndAngle=8.37758
    g2: ArcOfCircle CenterX=160.616 CenterY=40.7996 CenterZ=0 NormalX=0 NormalY=0 NormalZ=1 AngleXU=0 Radius=152.4 StartAngle=2.93956 EndAngle=3.11406
    g3: ArcOfCircle CenterX=2.66152 CenterY=45.1493 CenterZ=0 NormalX=0 NormalY=0 NormalZ=1 AngleXU=0 Radius=5.61439 StartAngle=3.24687 EndAngle=6.25565
    g4: ArcOfCircle CenterX=-64.9763 CenterY=38.002 CenterZ=0 NormalX=0 NormalY=0 NormalZ=1 AngleXU=0 Radius=62.4 StartAngle=0.10528 EndAngle=0.405315
    g5: ArcOfCircle CenterX=-5.42652 CenterY=63.5532 CenterZ=0 NormalX=0 NormalY=0 NormalZ=1 AngleXU=0 Radius=2.4 StartAngle=2.0944 EndAngle=3.54691
    g6: LineSegment StartX=-7.63206 StartY=62.6068 StartZ=0 EndX=-9.83761 EndY=61.6605 EndZ=0
    g7: LineSegment StartX=11.3157 StartY=71.3802 StartZ=0 EndX=13.6669 EndY=70.8987 EndZ=0
    g8: LineSegment StartX=2.70918 StartY=34.735 StartZ=0 EndX=2.68721 EndY=39.5349 EndZ=0
  constraints (25):
    c: Tangent(g0,g1) = 1.5708
    c: Tangent(g1,g2) = 1.5708
    c: Tangent(g2,g3) = 1.5708
    c: Tangent(g3,g4) = 1.5708
    c: Tangent(g4,g5) = 1.5708
    c: Tangent(g0,g5) = 1.5708
    c: Coincident(g4,g-3)
    c: Coincident(g2,g-4)
    c: Equal(g1,g5)
    c: PointOnObject(g-3,g0)
    c: PointOnObject(g-4,g0)
    c: Coincident(g6,g4)
    c: PointOnObject(g6,g-3)
    c: PointOnObject(g4,g6)
    c: Coincident(g7,g1)
    c: PointOnObject(g7,g-4)
    c: PointOnObject(g2,g7)
    c: Equal(g6,g7)
    c: Radius(g5) = 2.4
    c: Distance(g6) = 2.4
    c: PointOnObject(g8,g-5)
    c: PointOnObject(g8,g3)
    c: PointOnObject(g3,g8)
    c: PointOnObject(g-5,g8)
    c: Distance(g8) = 4.8
FEATURE [Sketcher::SketchObject] Sketch018
  ExternalGeometry = -> [Sketch014]
  FullyConstrained = true
  MapMode = 5
  Placement = pos=(0,0,0) rot=(0.57735,0.57735,0.57735;2.0944rad)
  Support = -> [YZ_Plane004]
  sketch-geometry (7):
    g0: LineSegment StartX=12.9956 StartY=86.8909 StartZ=0 EndX=18.1918 EndY=89.8909 EndZ=0
    g1: LineSegment StartX=18.1918 StartY=89.8909 StartZ=0 EndX=18.7918 EndY=88.8517 EndZ=0
    g2: LineSegment StartX=18.7918 StartY=88.8517 StartZ=0 EndX=17.7526 EndY=88.2517 EndZ=0
    g3: LineSegment StartX=17.7526 StartY=88.2517 StartZ=0 EndX=19.0526 EndY=86 EndZ=0
    g4: LineSegment StartX=19.0526 StartY=86 StartZ=0 EndX=14.8956 EndY=83.6 EndZ=0
    g5: LineSegment StartX=12.9956 StartY=86.8909 StartZ=0 EndX=14.8956 EndY=83.6 EndZ=0
    g6: LineSegment StartX=12.9956 StartY=86.8909 StartZ=0 EndX=7.79948 EndY=83.8909 EndZ=0
  constraints (21):
    c: Coincident(g0,g1)
    c: Coincident(g1,g2)
    c: Coincident(g2,g3)
    c: Coincident(g3,g4)
    c: Coincident(g5,g0)
    c: Perpendicular(g1,g0)
    c: Perpendicular(g2,g1)
    c: Perpendicular(g3,g2)
    c: Perpendicular(g4,g3)
    c: Distance(g1) = 1.2
    c: Equal(g1,g2)
    c: Coincident(g5,g4)
    c: Perpendicular(g4,g5)
    c: Perpendicular(g3,g-3) = 1.5708
    c: Distance(g3) = 2.6
    c: Distance(g4) = 4.8
    c: Distance(g3,g-3) = 8
    c: Coincident(g6,g0)
    c: Parallel(g6,g0)
    c: Equal(g6,g0)
    c: Distance(g0) = 6
FEATURE [PartDesign::Plane] DatumPlane004
  AttachmentOffset = pos=(0,0,4.8) rot=(0,0,1;0rad)
  Length = 60.9545
  MapMode = 5
  Placement = pos=(0,0,4.8) rot=(0,0,1;0rad)
  ResizeMode = 0
  Support = -> [XY_Plane004]
  Width = 70.9545
FEATURE [Sketcher::SketchObject] Sketch017
  FullyConstrained = true
  MapMode = 5
  Placement = pos=(0,0,4.8) rot=(0,0,1;0rad)
  Support = -> [DatumPlane004]
  sketch-geometry (2):
    g0: Circle CenterX=0 CenterY=24 CenterZ=0 NormalX=0 NormalY=0 NormalZ=1 AngleXU=0 Radius=2.4
    g1: Circle CenterX=0 CenterY=-24 CenterZ=0 NormalX=0 NormalY=0 NormalZ=1 AngleXU=0 Radius=2.4
  constraints (5):
    c: PointOnObject(g0,g-2)
    c: Equal(g1,g0)
    c: Symmetric(g1,g0,g-1)
    c: DistanceY(g1,g-1) = 24
    c: Radius(g0) = 2.4
FEATURE [PartDesign::Hole] Hole002
  BaseFeature = -> Pad007
  Depth = 25
  DepthType = 0
  Diameter = 5.5
  DrillForDepth = false
  DrillPoint = 1
  DrillPointAngle = 118
  HoleCutCountersinkAngle = 90
  HoleCutCustomValues = false
  HoleCutDepth = 0
  HoleCutDiameter = 7
  HoleCutType = 0
  ModelActualThread = false
  Placement = pos=(0,0,0) rot=(0.57735,0.57735,0.57735;2.0944rad)
  Profile = -> Sketch017
  Refine = true
  Tapered = false
  TaperedAngle = 90
  ThreadAngle = 0
  ThreadClass = 0
  ThreadCutOffInner = 0
  ThreadCutOffOuter = 0
  ThreadDirection = 0
  ThreadFit = 0
  ThreadPitch = 0
  ThreadSize = 13
  ThreadType = 1
  Threaded = false
FEATURE [PartDesign::Pocket] Pocket009
  BaseFeature = -> Hole002
  Length = 5
  Length2 = 100
  Midplane = true
  Placement = pos=(0,0,0) rot=(0.57735,0.57735,0.57735;2.0944rad)
  Profile = -> Sketch016
  Refine = true
  Type = 1
FEATURE [PartDesign::Pocket] Pocket010
  BaseFeature = -> Pocket009
  Length = 5
  Length2 = 100
  Midplane = true
  Placement = pos=(0,0,0) rot=(0.57735,0.57735,0.57735;2.0944rad)
  Profile = -> Sketch015
  Refine = true
  Type = 1
FEATURE [PartDesign::Pad] Pad008
  BaseFeature = -> Pocket010
  Direction = (1,1,1)
  Length = 10
  Length2 = 100
  Midplane = true
  Placement = pos=(0,0,0) rot=(0.57735,0.57735,0.57735;2.0944rad)
  Profile = -> Sketch018
  Refine = true
  Type = 0
FEATURE [PartDesign::LinearPattern] LinearPattern002
  BaseFeature = -> Pad008
  Direction = -> Sketch018 [Axis0]
  Length = 40
  Occurrences = 2
  Originals = -> [Pad008]
  Placement = pos=(0,0,0) rot=(0.57735,0.57735,0.57735;2.0944rad)
  Refine = true
FEATURE [PartDesign::Fillet] Fillet002
  Base = -> LinearPattern002 [Edge36,Edge8,Edge39,Edge59,Edge4,Edge3,Edge33,Edge32,Edge55,Edge56,Edge47,Edge48]
  BaseFeature = -> LinearPattern002
  Placement = pos=(0,0,0) rot=(0.57735,0.57735,0.57735;2.0944rad)
  Radius = 2.4
  Refine = true
  SupportTransform = false
FEATURE [PartDesign::Body] Body002  label="Support"
  Group = -> [Sketch014,Pad007,Sketch016,Sketch017,DatumPlane004,Hole002,Pocket009,Sketch015,Pocket010,Sketch018,Pad008,LinearPattern002,Fillet002]
  Origin = -> Origin025
  Placement = pos=(30,-36.4,-88) rot=(-1,0,0;0.523599rad)
  Tip = -> Fillet002
FEATURE [Sketcher::SketchObject] Sketch019
  FullyConstrained = true
  MapMode = 5
  Placement = pos=(0,0,-20.6) rot=(0,0,1;0rad)
  Support = -> [DatumPlane003]
  sketch-geometry (5):
    g0: LineSegment StartX=24.8 StartY=16.8 StartZ=0 EndX=35.2 EndY=16.8 EndZ=0
    g1: LineSegment StartX=35.2 StartY=16.8 StartZ=0 EndX=35.2 EndY=23.2 EndZ=0
    g2: LineSegment StartX=35.2 StartY=23.2 StartZ=0 EndX=24.8 EndY=23.2 EndZ=0
    g3: LineSegment StartX=24.8 StartY=23.2 StartZ=0 EndX=24.8 EndY=16.8 EndZ=0
    g4: GeomPoint X=30 Y=20 Z=0
  constraints (13):
    c: Coincident(g0,g1)
    c: Coincident(g1,g2)
    c: Coincident(g2,g3)
    c: Coincident(g3,g0)
    c: Horizontal(g0)
    c: Horizontal(g2)
    c: Vertical(g1)
    c: Vertical(g3)
    c: DistanceY(g3,g3) = 6.4
    c: DistanceX(g2,g2) = 10.4
    c: DistanceX(g4) = 30
    c: DistanceY(g4) = 20
    c: Symmetric(g0,g1,g4)
FEATURE [PartDesign::Pocket] Pocket011
  BaseFeature = -> LinearPattern001
  Length = 5
  Length2 = 100
  Placement = pos=(-76.85,-38.3,-27.1) rot=(0.707107,-0.707107,0;3.14159rad)
  Profile = -> Sketch019
  Refine = true
  Type = 1
FEATURE [PartDesign::Mirrored] Mirrored002
  MirrorPlane = -> Sketch019 [H_Axis]
  Placement = pos=(-76.85,-38.3,-27.1) rot=(0.707107,-0.707107,0;3.14159rad)
  Refine = true
FEATURE [PartDesign::Mirrored] Mirrored003
  MirrorPlane = -> YZ_Plane
  Placement = pos=(-76.85,-38.3,-27.1) rot=(0.707107,-0.707107,0;3.14159rad)
  Refine = true
FEATURE [PartDesign::MultiTransform] MultiTransform001
  BaseFeature = -> Pocket011
  Originals = -> [Pocket011]
  Placement = pos=(-76.85,-38.3,-27.1) rot=(0.707107,-0.707107,0;3.14159rad)
  Refine = true
  Transformations = -> [Mirrored002,Mirrored003]
FEATURE [PartDesign::Body] Body  label="Boîtier inférieur"
  Group = -> [Binder,Sketch,Pad,Sketch001,Pocket,Sketch002,Pocket001,Binder001,Sketch003,Pad001,Sketch004,Pad002,DatumPlane,Sketch005,Pocket002,Sketch006,Pocket003,LinearPattern,Chamfer,Binder008,Binder009,Binder010,Binder011,Binder012,DatumPlane003,Sketch012,Pad006,Sketch013,Pocket008,Sphere,Fillet001,LinearPattern001,Sketch019,Pocket011,MultiTransform001,Mirrored002,Mirrored003]
  Origin = -> Origin021
  Tip = -> MultiTransform001
FEATURE [Part::FeaturePython] Standoff001  label="M3x3-Standoff"  # WARN: FeaturePython — macro-defined, semantics opaque (R4)
  Placement = pos=(-79.65,-20.55,-23) rot=(0,0,1;0rad)
  baseObject = -> Body [Edge46]
  blind = false
  diameter = 1
  invert = false
  length = 0
  offset = 0
FEATURE [Part::FeaturePython] Standoff002  label="M3x3-Standoff"  # WARN: FeaturePython — macro-defined, semantics opaque (R4)
  Placement = pos=(-78.5,-57.45,0) rot=(0,0,1;0rad)
  baseObject = -> Body [Edge45]
  blind = false
  diameter = 1
  invert = false
  length = 0
  offset = 0
FEATURE [Part::FeaturePython] Standoff003  label="M3x3-Standoff"  # WARN: FeaturePython — macro-defined, semantics opaque (R4)
  Placement = pos=(78.5,57.45,1.07e-14) rot=(0,0,1;0rad)
  baseObject = -> MultiTransform001 [Edge140]
  blind = false
  diameter = 1
  invert = false
  length = 0
  offset = 0
FEATURE [Part::FeaturePython] Standoff004  label="M3x3-Standoff"  # WARN: FeaturePython — macro-defined, semantics opaque (R4)
  Placement = pos=(78.5,-57.45,7.1e-15) rot=(0,0,1;0rad)
  baseObject = -> MultiTransform001 [Edge153]
  blind = false
  diameter = 1
  invert = false
  length = 0
  offset = 0
FEATURE [App::Part] Part021  label="Ensemble boîtier inf"
  Group = -> [Standoff003,Standoff001,Standoff004,Standoff002,Body]
  Origin = -> Origin023
FEATURE [PartDesign::FeatureBase] Clone
  BaseFeature = -> Body002
  Placement = pos=(20,-36.4,-88) rot=(-1,0,0;0.523599rad)
FEATURE [PartDesign::Body] Body003  label="Support2"
  BaseFeature = -> Body002
  Group = -> [Clone]
  Origin = -> Origin026
  Placement = pos=(-50,0,0) rot=(0,0,1;0rad)
  Tip = -> Clone
FEATURE [Mesh::Feature] Mesh  label="Support (Meshed)"
FEATURE [App::Part] Part023  label="Supports"
  Group = -> [Body002,Body003]
  Origin = -> Origin027
FEATURE [Mesh::Feature] Mesh008  label="Boîtier inférieur (Meshed)001"
FEATURE [App::DocumentObjectGroup] Groupe001  label="Maillages"
  Group = -> [Mesh004,Mesh,Mesh008]
note: 2 file-system paths scrubbed to <path> (originals preserved in the JSON sidecar)
